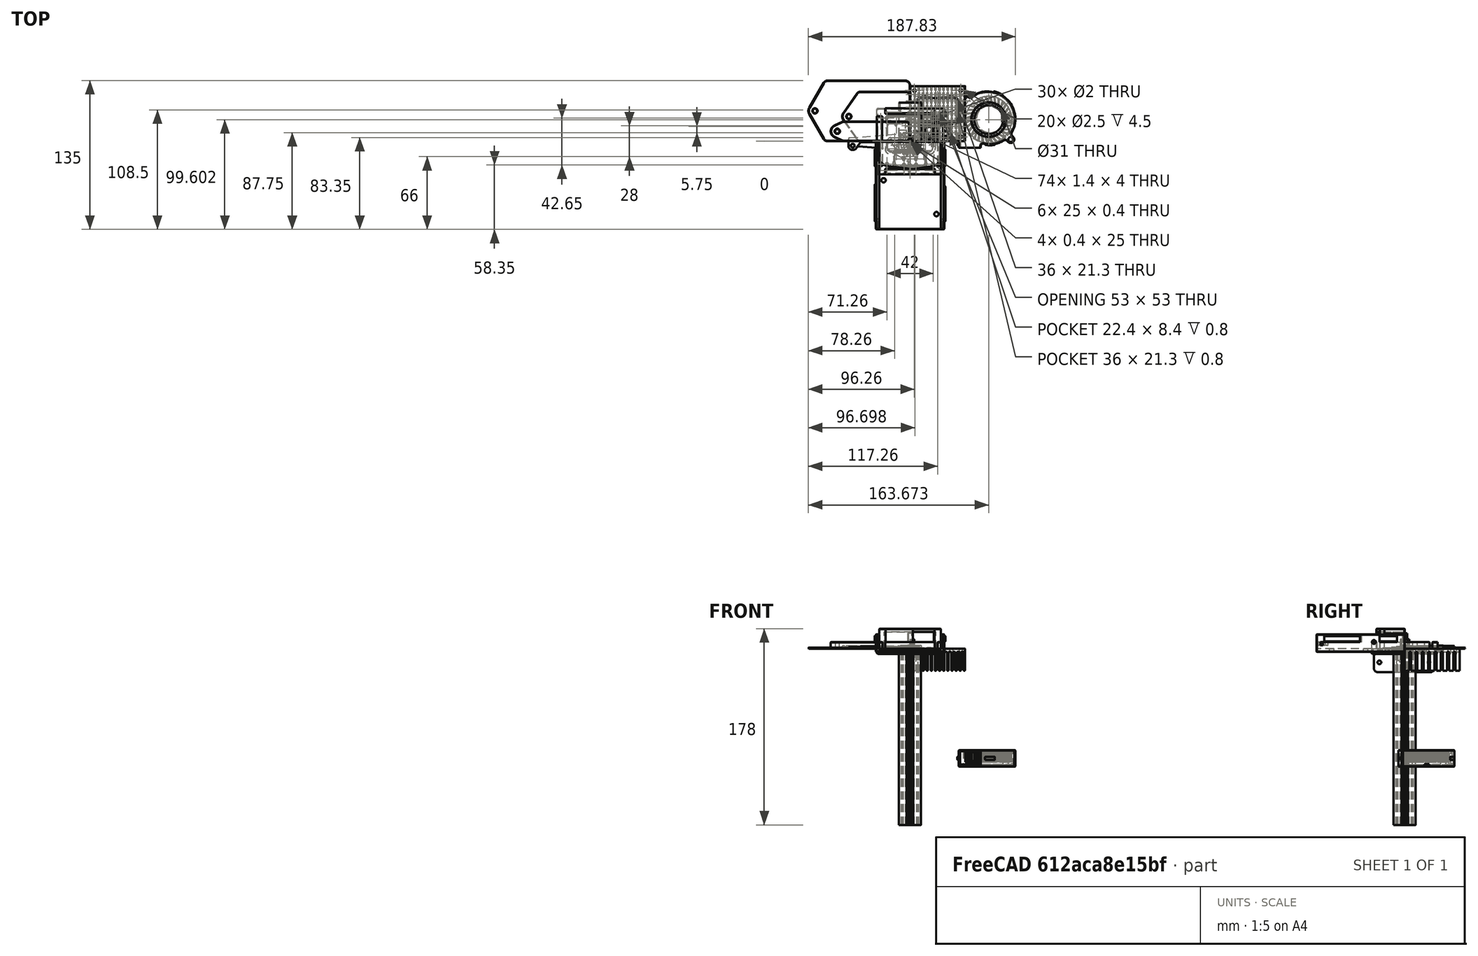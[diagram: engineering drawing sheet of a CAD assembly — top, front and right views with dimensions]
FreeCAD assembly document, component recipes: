
FREECAD ASSEMBLY — COMPONENT RECIPES ("bedburner")

This assembly document has 27 components, labeled P0..P26 below (a component is one placed body or linked part). 7 of them carry a construction recipe — the FreeCAD feature program that regenerates the part from scratch, quoted from this document or its linked companion documents; the rest are supplied as boundary geometry only. No exploded tour is included for this assembly.
COMPONENT P0 — geometry summary ("HFS5-2020-161"; no construction recipe available for this part):
  bounding box: 160.0 x 20.0 x 20.0 mm
  tessellated surface: 1,048 triangles
  volume: 29141 mm^3 (46% of its bounding box)
  symmetry: 2-fold rotationally symmetric about the x axis; 4-fold rotationally symmetric about the y axis; 2-fold rotationally symmetric about the z axis; mirror-symmetric across its x mid-plane, y mid-plane, z mid-plane
COMPONENT P1 — geometry summary ("fan_radial_50x016"; no construction recipe available for this part):
  bounding box: 55.3 x 54.7 x 15.0 mm
  tessellated surface: 21,378 triangles
  volume: 17025 mm^3 (37% of its bounding box)
COMPONENT P2 — recipe-attached ("heater_bracket001", modeled in this document).
Construction recipe (the document's own serialized feature program — sketch geometry with constraints, then the solid features built on it; lengths are millimeters unless a unit is written):

FEATURE [Sketcher::SketchObject] Sketch085  label="hrb_block_plate_s"
  ArcFitTolerance = 0
  AttachmentSupport = -> [XY_Plane138]
  ExternalTypes = [0]
  FullyConstrained = true
  MakeInternals = false
  MapMode = 5
  _ExternalGeoVersion = 0
  expr: .Constraints.bend_straight = <<bracket_params>>.feature_bend_straight
  expr: .Constraints.block_screw_spacing = <<block_params>>.heatsink_screw_spacing
  expr: .Constraints.block_side_offset = <<bracket_params>>.feature_block_offset
  expr: .Constraints.block_width = <<block_params>>.heatsink_width
  expr: .Constraints.height_block_bottom = <<bracket_params>>.feature_deck_clear_block
  expr: .Constraints.height_block_top = <<bracket_params>>.feature_deck_clear_block + <<block_params>>.heatsink_height
  expr: .Constraints.height_bracket_bottom = <<bracket_params>>.feature_deck_clear_bracket
  expr: .Constraints.height_component_top = <<bracket_params>>.feature_deck_clear_block + <<block_params>>.heatsink_height + <<bracket_params>>.height_componets
  expr: .Constraints.height_extrusion = <<bracket_params>>.height_extrusion
  expr: .Constraints.height_stock_bed = <<bracket_params>>.height_extrusion + <<bracket_params>>.height_stock
  expr: .Constraints.height_stock_silicone = <<bracket_params>>.height_extrusion + <<bracket_params>>.height_stock - <<bracket_params>>.height_silicone_heater
  expr: .Constraints.height_whop_bed = <<bracket_params>>.height_extrusion + <<bracket_params>>.height_whopKinematic
  expr: .Constraints.height_whop_silicone = <<bracket_params>>.height_extrusion + <<bracket_params>>.height_whopKinematic - <<bracket_params>>.height_silicone_heater
  expr: .Constraints.plate_block_overlap = <<bracket_params>>.rear_overlap
  expr: .Constraints.plate_overhang = <<bracket_params>>.rear_overhang_inner
  expr: .Constraints.plate_overhang_outer = <<bracket_params>>.rear_overhang_outer
  expr: .Constraints.screw_head = <<bracket_params>>.feature_screw_head
  expr: .Constraints.screw_hole = <<bracket_params>>.feature_screw_hole
  expr: .Constraints.screw_pad_diam = <<bracket_params>>.rear_pad_diam
  expr: .Constraints.side_extension = <<bracket_params>>.rear_side_extension
  expr: .Constraints.side_screw_inset1 = <<bracket_params>>.rear_side_screw_inset
  expr: .Constraints.side_screw_inset2 = <<bracket_params>>.rear_side_screw_inset + <<bracket_params>>.rear_side_screw_spacing
  sketch-geometry (50):
    g0: Circle CenterX=-10 CenterY=-4 CenterZ=0 NormalX=0 NormalY=0 NormalZ=1 AngleXU=0 Radius=1.7
    g1: Circle CenterX=-52 CenterY=-4 CenterZ=0 NormalX=0 NormalY=0 NormalZ=1 AngleXU=0 Radius=1.7
    g2: ArcOfCircle CenterX=-52 CenterY=-4 CenterZ=0 NormalX=0 NormalY=0 NormalZ=1 AngleXU=0 Radius=4 StartAngle=3.14159 EndAngle=5.67232
    g3: ArcOfCircle CenterX=-10 CenterY=-4 CenterZ=0 NormalX=0 NormalY=0 NormalZ=1 AngleXU=0 Radius=4 StartAngle=3.75246 EndAngle=6.28319
    g4: LineSegment [constr] StartX=-52 StartY=-2.3 StartZ=0 EndX=-52 EndY=0 EndZ=0
    g5: LineSegment StartX=-48.7234 StartY=-6.29431 StartZ=0 EndX=-45.0163 EndY=-1 EndZ=0
    g6: LineSegment StartX=-13.2766 StartY=-6.29431 StartZ=0 EndX=-16.9837 EndY=-1 EndZ=0
    g7: LineSegment StartX=-56 StartY=-4 StartZ=0 EndX=-56 EndY=3 EndZ=0
    g8: LineSegment StartX=-45.0163 StartY=-1 StartZ=0 EndX=-16.9837 EndY=-1 EndZ=0
    g9: LineSegment StartX=-6 StartY=-1 StartZ=0 EndX=-6 EndY=-4 EndZ=0
    g10: LineSegment StartX=-6 StartY=-1 StartZ=0 EndX=0 EndY=-1 EndZ=0
    g11: LineSegment StartX=0 StartY=-1 StartZ=0 EndX=0 EndY=7 EndZ=0
    g12: LineSegment [constr] StartX=0 StartY=0 StartZ=0 EndX=20 EndY=0 EndZ=0
    g13: LineSegment [constr] StartX=20 StartY=0 StartZ=0 EndX=20 EndY=-20 EndZ=0
    g14: LineSegment [constr] StartX=20 StartY=-20 StartZ=0 EndX=0 EndY=-20 EndZ=0
    g15: LineSegment [constr] StartX=0 StartY=-20 StartZ=0 EndX=0 EndY=0 EndZ=0
    g16: Circle [constr] CenterX=10 CenterY=-10 CenterZ=0 NormalX=0 NormalY=0 NormalZ=1 AngleXU=0 Radius=10
    g17: LineSegment [constr] StartX=29.5 StartY=0 StartZ=0 EndX=29.5 EndY=-20 EndZ=0
    g18: LineSegment [constr] StartX=35.5 StartY=0 StartZ=0 EndX=35.5 EndY=-20 EndZ=0
    g19: LineSegment [constr] StartX=29.5 StartY=-20 StartZ=0 EndX=27.5 EndY=-20 EndZ=0
    g20: LineSegment [constr] StartX=27.5 StartY=-20 StartZ=0 EndX=27.5 EndY=-10 EndZ=0
    g21: LineSegment [constr] StartX=35.5 StartY=-20 StartZ=0 EndX=33.5 EndY=-20 EndZ=0
    g22: LineSegment [constr] StartX=33.5 StartY=-20 StartZ=0 EndX=33.5 EndY=-10 EndZ=0
    g23: Circle [constr] CenterX=0 CenterY=5 CenterZ=0 NormalX=0 NormalY=0 NormalZ=1 AngleXU=0 Radius=1.7
    g24: Circle [constr] CenterX=0 CenterY=5 CenterZ=0 NormalX=0 NormalY=0 NormalZ=1 AngleXU=0 Radius=2.75
    g25: Circle [constr] CenterX=0 CenterY=22 CenterZ=0 NormalX=0 NormalY=0 NormalZ=1 AngleXU=0 Radius=1.7
    g26: Circle [constr] CenterX=0 CenterY=22 CenterZ=0 NormalX=0 NormalY=0 NormalZ=1 AngleXU=0 Radius=2.75
    g27: LineSegment [constr] StartX=0 StartY=27 StartZ=0 EndX=0 EndY=23.7 EndZ=0
    g28: LineSegment StartX=-56 StartY=3 StartZ=0 EndX=-4 EndY=7 EndZ=0
    g29: LineSegment StartX=-4 StartY=7 StartZ=0 EndX=0 EndY=7 EndZ=0
    g30: LineSegment [constr] StartX=-56 StartY=0 StartZ=0 EndX=-56 EndY=-50 EndZ=0
    g31: LineSegment [constr] StartX=-56 StartY=-50 StartZ=0 EndX=-6 EndY=-50 EndZ=0
    g32: LineSegment [constr] StartX=-6 StartY=-50 StartZ=0 EndX=-6 EndY=0 EndZ=0
    g33: LineSegment [constr] StartX=-6 StartY=0 StartZ=0 EndX=-56 EndY=0 EndZ=0
    g34: LineSegment [constr] StartX=-52 StartY=-4 StartZ=0 EndX=-52 EndY=-46 EndZ=0
    g35: LineSegment [constr] StartX=-52 StartY=-46 StartZ=0 EndX=-10 EndY=-46 EndZ=0
    g36: LineSegment [constr] StartX=-10 StartY=-46 StartZ=0 EndX=-10 EndY=-4 EndZ=0
    g37: LineSegment [constr] StartX=-10 StartY=-4 StartZ=0 EndX=-52 EndY=-4 EndZ=0
    g38: Circle [constr] CenterX=-31 CenterY=-25 CenterZ=0 NormalX=0 NormalY=0 NormalZ=1 AngleXU=0 Radius=21
    g39: Circle [constr] CenterX=-31 CenterY=-25 CenterZ=0 NormalX=0 NormalY=0 NormalZ=1 AngleXU=0 Radius=25
    g40: Circle [constr] CenterX=-10 CenterY=-4 CenterZ=0 NormalX=0 NormalY=0 NormalZ=1 AngleXU=0 Radius=2.75
    g41: Circle [constr] CenterX=-52 CenterY=-4 CenterZ=0 NormalX=0 NormalY=0 NormalZ=1 AngleXU=0 Radius=2.75
    g42: LineSegment [constr] StartX=29 StartY=0 StartZ=0 EndX=22.5 EndY=0 EndZ=0
    g43: LineSegment [constr] StartX=22.5 StartY=-10 StartZ=0 EndX=29 EndY=-10 EndZ=0
    g44: LineSegment [constr] StartX=29 StartY=-10 StartZ=0 EndX=29 EndY=0 EndZ=0
    g45: LineSegment [constr] StartX=2.5 StartY=0 StartZ=0 EndX=2.5 EndY=-20 EndZ=0
    g46: LineSegment [constr] StartX=2.5 StartY=-20 StartZ=0 EndX=22.5 EndY=-20 EndZ=0
    g47: LineSegment [constr] StartX=22.5 StartY=-20 StartZ=0 EndX=22.5 EndY=0 EndZ=0
    g48: LineSegment [constr] StartX=22.5 StartY=0 StartZ=0 EndX=2.5 EndY=0 EndZ=0
    g49: LineSegment [constr] StartX=1 StartY=0 StartZ=0 EndX=1 EndY=-20 EndZ=0
  constraints (147):
    c: Equal(g0,g1)
    c: Diameter(g1) = 3.4  'screw_hole'
    c: Coincident(g2,g1)
    c: Coincident(g3,g0)
    c: Equal(g2,g3)
    c: PointOnObject(g4,g1)
    c: PointOnObject(g4,g2)
    c: Vertical(g4)
    c: PointOnObject(g1,g4)
    c: Diameter(g2) = 8  'screw_pad_diam'
    c: Vertical(g7)
    c: Tangent(g7,g2) = 1.5708
    c: Tangent(g2,g5) = -1.5708
    c: Tangent(g6,g3) = 1.5708
    c: Coincident(g8,g5)
    c: Coincident(g8,g6)
    c: Horizontal(g8)
    c: Equal(g5,g6)
    c: Angle(g5,g7) = 0.610865  'screw_pad_angle'
    c: Distance(g8) = 28.0326  'plate_overlay_width'
    c: Vertical(g9)
    c: Coincident(g10,g9)
    c: PointOnObject(g10,g-2)
    c: Horizontal(g10)
    c: Tangent(g9,g3) = 1.5708
    c: Coincident(g11,g10)
    c: PointOnObject(g11,g-2)
    c: DistanceY(g-1,g11) = 7  'plate_overhang'
    c: PointOnObject(g10,g8)
    c: Coincident(g12,g13)
    c: Coincident(g13,g14)
    c: Coincident(g14,g15)
    c: Coincident(g15,g12)
    c: Horizontal(g12)
    c: Horizontal(g14)
    c: Vertical(g13)
    c: Vertical(g15)
    c: Tangent(g15,g16)
    c: Tangent(g16,g12)
    c: Tangent(g16,g13)
    c: Tangent(g14,g16)
    c: Distance(g14) = 20  'height_extrusion'
    c: Vertical(g17)
    c: Vertical(g18)
    c: PointOnObject(g17,g14)
    c: PointOnObject(g18,g14)
    c: PointOnObject(g17,g12)
    c: PointOnObject(g18,g12)
    c: Coincident(g19,g17)
    c: Coincident(g20,g19)
    c: Coincident(g21,g18)
    c: Coincident(g22,g21)
    c: Vertical(g22)
    c: Horizontal(g21)
    c: Horizontal(g19)
    c: Coincident(g24,g23)
    c: Coincident(g26,g25)
    c: Equal(g23,g25)
    c: Equal(g26,g24)
    c: Equal(g23,g0)
    c: PointOnObject(g25,g-2)
    c: PointOnObject(g23,g-2)
    c: PointOnObject(g27,g25)
    c: PointOnObject(g27,g-2)
    c: PointOnObject(g27,g-2)
    c: Distance(g27) = 3.3  'side_screw_outer'
    c: DistanceY(g11,g27) = 20  'side_extension'
    c: Coincident(g7,g28)
    c: Coincident(g28,g29)
    c: Coincident(g29,g11)
    c: Horizontal(g29)
    c: DistanceX(g29,g29) = 4  'bend_straight'
    c: Coincident(g30,g31)
    c: Coincident(g31,g32)
    c: Coincident(g32,g33)
    c: Coincident(g33,g30)
    c: Vertical(g30)
    c: Vertical(g32)
    c: Horizontal(g31)
    c: Horizontal(g33)
    c: Coincident(g34,g35)
    c: Coincident(g35,g36)
    c: Coincident(g36,g37)
    c: Coincident(g37,g34)
    c: Vertical(g34)
    c: Vertical(g36)
    c: Horizontal(g35)
    c: Horizontal(g37)
    c: Coincident(g39,g38)
    c: Tangent(g39,g33)
    c: Tangent(g39,g32)
    c: Tangent(g39,g31)
    c: Tangent(g39,g30)
    c: Diameter(g39) = 50  'block_width'
    c: Tangent(g37,g38)
    c: Tangent(g38,g36)
    c: Tangent(g38,g35)
    c: Tangent(g38,g34)
    c: Diameter(g38) = 42  'block_screw_spacing'
    c: Distance(g6,g-1) = 1  'plate_block_overlap'
    c: DistanceY(g-1,g7) = 3  'plate_overhang_outer'
    c: Coincident(g34,g1)
    c: Coincident(g36,g0)
    c: PointOnObject(g32,g-1)
    c: Distance(g32,g-1) = 6  'block_side_offset'
    c: Coincident(g40,g0)
    c: Coincident(g41,g1)
    c: Equal(g24,g40)
    c: Equal(g40,g41)
    c: Diameter(g41) = 5.5  'screw_head'
    c: DistanceY(g-1,g23) = 5  'side_screw_inset1'
    c: DistanceY(g-1,g25) = 22  'side_screw_inset2'
    c: Coincident(g12,g-1)
    c: DistanceX(g-1,g17) = 29.5  'height_stock_bed'
    c: DistanceX(g-1,g19) = 27.5  'height_stock_silicone'
    c: DistanceX(g-1,g21) = 33.5  'height_whop_silicone'
    c: DistanceX(g-1,g18) = 35.5  'height_whop_bed'
    c: Coincident(g43,g44)
    c: Coincident(g44,g42)
    c: Horizontal(g42)
    c: Horizontal(g43)
    c: Vertical(g44)
    c: PointOnObject(g20,g43)
    c: PointOnObject(g22,g43)
    c: PointOnObject(g16,g43)
    c: PointOnObject(g42,g-1)
    c: Coincident(g45,g46)
    c: Coincident(g46,g47)
    c: Coincident(g47,g48)
    c: Coincident(g48,g45)
    c: Vertical(g45)
    c: Vertical(g47)
    c: Horizontal(g46)
    c: Horizontal(g48)
    c: Coincident(g47,g42)
    c: PointOnObject(g43,g47)
    c: Vertical(g49)
    c: PointOnObject(g49,g12)
    c: PointOnObject(g49,g14)
    c: DistanceX(g-1,g45) = 2.5  'height_block_bottom'
    c: PointOnObject(g45,g14)
    c: DistanceX(g-1,g49) = 1  'height_bracket_bottom'
    c: DistanceX(g-1,g46) = 22.5  'height_block_top'
    c: DistanceX(g-1,g43) = 29  'height_component_top'
    c: DistanceX(g43,g22) = 4.5  'height_clear_whop'
    c: DistanceX(g19,g43) = 1.5  'height_crash_stock'
    c: Vertical(g20)
FEATURE [Sketcher::SketchObject] Sketch086  label="hrb_side_features_s"
  ArcFitTolerance = 0
  AttachmentSupport = -> [YZ_Plane138]
  ExternalTypes = [0]
  FullyConstrained = true
  MakeInternals = false
  MapMode = 5
  Placement = pos=(0,0,0) rot=(0.57735,0.57735,0.57735;2.0944rad)
  _ExternalGeoVersion = 0
  expr: .Constraints.cut_end = <<bracket_params>>.rear_overhang_inner + <<bracket_params>>.rear_side_extension + 1 mm
  expr: .Constraints.plate_overhang = <<bracket_params>>.rear_overhang_inner
  expr: .Constraints.screw_head = <<bracket_params>>.feature_screw_head
  expr: .Constraints.screw_height = <<bracket_params>>.feature_side_height + <<bracket_params>>.feature_deck_clear_bracket - <<bracket_params>>.height_extrusion / 2
  expr: .Constraints.screw_hole = <<bracket_params>>.feature_screw_hole
  expr: .Constraints.screw_inset1 = <<bracket_params>>.rear_side_screw_inset
  expr: .Constraints.screw_inset2 = <<bracket_params>>.rear_side_screw_inset + <<bracket_params>>.rear_side_screw_spacing
  expr: .Constraints.side_recess_top = <<bracket_params>>.feature_side_height + <<bracket_params>>.feature_deck_clear_bracket - <<bracket_params>>.height_extrusion + <<bracket_params>>.feature_side_recess
  sketch-geometry (9):
    g0: Circle CenterX=5 CenterY=-12.5 CenterZ=0 NormalX=0 NormalY=0 NormalZ=1 AngleXU=0 Radius=1.7
    g1: Circle CenterX=22 CenterY=-12.5 CenterZ=0 NormalX=0 NormalY=0 NormalZ=1 AngleXU=0 Radius=1.7
    g2: LineSegment [constr] StartX=5 StartY=-12.5 StartZ=0 EndX=22 EndY=-12.5 EndZ=0
    g3: Circle [constr] CenterX=5 CenterY=-12.5 CenterZ=0 NormalX=0 NormalY=0 NormalZ=1 AngleXU=0 Radius=2.75
    g4: Circle [constr] CenterX=22 CenterY=-12.5 CenterZ=0 NormalX=0 NormalY=0 NormalZ=1 AngleXU=0 Radius=2.75
    g5: LineSegment StartX=28 StartY=-3.5 StartZ=0 EndX=28 EndY=0 EndZ=0
    g6: LineSegment StartX=7 StartY=0 StartZ=0 EndX=7 EndY=-3.5 EndZ=0
    g7: LineSegment StartX=7 StartY=-3.5 StartZ=0 EndX=28 EndY=-3.5 EndZ=0
    g8: LineSegment StartX=7 StartY=0 StartZ=0 EndX=28 EndY=0 EndZ=0
  constraints (24):
    c: Coincident(g2,g0)
    c: Coincident(g2,g1)
    c: Horizontal(g2)
    c: Diameter(g0) = 3.4  'screw_hole'
    c: Equal(g1,g0)
    c: Coincident(g3,g0)
    c: Coincident(g4,g1)
    c: Diameter(g3) = 5.5  'screw_head'
    c: Equal(g3,g4)
    c: Coincident(g6,g7)
    c: Coincident(g7,g5)
    c: Vertical(g5)
    c: Vertical(g6)
    c: Horizontal(g7)
    c: PointOnObject(g5,g-1)
    c: Coincident(g8,g6)
    c: PointOnObject(g6,g-1)
    c: DistanceX(g-1,g6) = 7  'plate_overhang'
    c: Coincident(g8,g5)
    c: DistanceX(g-1,g5) = 28  'cut_end'
    c: DistanceY(g0,g-1) = 12.5  'screw_height'
    c: DistanceX(g-1,g0) = 5  'screw_inset1'
    c: DistanceX(g-1,g1) = 22  'screw_inset2'
    c: DistanceY(g6,g-1) = 3.5  'side_recess_top'
FEATURE [PartDesign::FeaturePython] BaseBend  label="hrb_block_plate"  # WARN: FeaturePython — macro-defined, semantics opaque (R4)
  BendSide = 0
  BendSketch = -> Sketch085
  MidPlane = false
  Reverse = false
  Suppressed = false
  length = 100
  radius = 1.6
  thickness = 1.5
  expr: radius = <<bracket_params>>.material_bend
  expr: thickness = <<bracket_params>>.material_thickness
FEATURE [PartDesign::FeaturePython] Bend  label="hrb_side_bend"  # WARN: FeaturePython — macro-defined, semantics opaque (R4)
  AutoMiter = true
  BaseFeature = -> BaseBend
  BendType = 1
  LengthList = [21.5]
  LengthSpec = 2
  NonperforationMaxLength = 5
  Perforate = false
  PerforationAngle = 0
  PerforationInitialLength = 5
  PerforationMaxLength = 5
  ReliefFactor = 0.7
  Suppressed = false
  UseReliefFactor = false
  angle = 90
  baseObject = -> BaseBend [Edge27]
  bendAList = [90]
  extend1 = 0
  extend2 = 0
  gap1 = 0
  gap2 = 0
  invert = false
  kfactor = 0.5
  length = 21.5
  maxExtendDist = 5
  minGap = 0.2
  minReliefGap = 1
  miterangle1 = 0
  miterangle2 = 0
  offset = 0
  radius = 1.6
  reliefType = 0
  reliefd = 1
  reliefw = 0.8
  sketchflip = false
  sketchinvert = false
  unfold = false
  expr: length = <<bracket_params>>.feature_side_height
  expr: radius = <<bracket_params>>.material_bend
FEATURE [PartDesign::FeaturePython] Extend  label="hrb_side_ext"  # WARN: FeaturePython — macro-defined, semantics opaque (R4)
  BaseFeature = -> Bend
  Offset = 0.02
  Refine = true
  Suppressed = false
  UseSubtraction = false
  baseObject = -> Bend [Face21]
  gap1 = 0
  gap2 = 0
  length = 20
  expr: length = <<bracket_params>>.rear_side_extension
FEATURE [PartDesign::Pocket] Pocket  label="hrb_side_features"
  BaseFeature = -> Extend
  Direction = (-1,0,0)
  Length = 1.5
  Length2 = 5
  Profile = -> Sketch086
  ReferenceAxis = -> Sketch086 [N_Axis]
  Refine = true
  SideType = 0
  Suppressed = false
  Type = 0
  Type2 = 0
  expr: Length = <<bracket_params>>.material_thickness
FEATURE [PartDesign::Fillet] Fillet  label="hrb_outer_flt"
  Base = -> Pocket [Edge2]
  BaseFeature = -> Pocket
  Radius = 1.5
  Refine = true
  SupportTransform = false
  Suppressed = false
  UseAllEdges = false
FEATURE [PartDesign::Fillet] Fillet014  label="hrb_side_flt"
  Base = -> Fillet [Edge59,Edge46,Edge65]
  BaseFeature = -> Fillet
  Radius = 4
  Refine = true
  SupportTransform = false
  Suppressed = false
  UseAllEdges = false
FEATURE [PartDesign::Fillet] Fillet015  label="hrb_ext_flt"
  Base = -> Fillet014 [Edge62]
  BaseFeature = -> Fillet014
  Radius = 1.5
  Refine = true
  SupportTransform = false
  Suppressed = false
  UseAllEdges = false
FEATURE [PartDesign::Fillet] Fillet019  label="hrb_overlay_flt"
  Base = -> Fillet015 [Edge75,Edge76]
  BaseFeature = -> Fillet015
  Radius = 1.5
  Refine = true
  SupportTransform = false
  Suppressed = false
  UseAllEdges = false
FEATURE [PartDesign::Body] Body048  label="heater_rear_bracket"
  AllowCompound = false
  Group = -> [Sketch085,Sketch086,BaseBend,Bend,Extend,Pocket,Fillet,Fillet014,Fillet015,Fillet019]
  Origin = -> Origin138
  Tip = -> Fillet019
COMPONENT P3 — recipe-attached ("heater_fan_duct001", modeled in this document).
Construction recipe (the document's own serialized feature program — sketch geometry with constraints, then the solid features built on it; lengths are millimeters unless a unit is written):

FEATURE [Sketcher::SketchObject] Sketch  label="hfd_base_s"
  ArcFitTolerance = 1e-06
  AttachmentSupport = -> [XY_Plane140]
  ExternalTypes = [0]
  FullyConstrained = true
  MakeInternals = false
  MapMode = 5
  _ExternalGeoVersion = 0
  expr: .Constraints.base_width = <<block_params>>.heatsink_width + 2 * <<bracket_params>>.feature_block_offset
  expr: .Constraints.ref_block_spacing = <<bracket_params>>.feature_block_offset
  expr: .Constraints.ref_block_width = <<block_params>>.heatsink_width
  sketch-geometry (65):
    g0: LineSegment [constr] StartX=21.7128 StartY=-20.5407 StartZ=0 EndX=-28.635 EndY=-28.6713 EndZ=0
    g1: LineSegment [constr] StartX=-28.635 StartY=-28.6713 StartZ=0 EndX=-20.5044 EndY=-79.019 EndZ=0
    g2: LineSegment [constr] StartX=-20.5044 StartY=-79.019 StartZ=0 EndX=29.8433 EndY=-70.8884 EndZ=0
    g3: LineSegment [constr] StartX=29.8433 StartY=-70.8884 StartZ=0 EndX=21.7128 EndY=-20.5407 EndZ=0
    g4: LineSegment [constr] StartX=2.46216 StartY=-23.6495 StartZ=0 EndX=2.781 EndY=-25.6239 EndZ=0
    g5: Circle [constr] CenterX=24 CenterY=-66.1595 CenterZ=0 NormalX=0 NormalY=0 NormalZ=1 AngleXU=0 Radius=2.25
    g6: Circle [constr] CenterX=-24 CenterY=-35.4187 CenterZ=0 NormalX=0 NormalY=0 NormalZ=1 AngleXU=0 Radius=2.25
    g7: Circle [constr] CenterX=-1.38618 CenterY=-50 CenterZ=0 NormalX=0 NormalY=0 NormalZ=1 AngleXU=0 Radius=16.25
    g8: LineSegment [constr] StartX=-5.43552 StartY=-24.9249 StartZ=0 EndX=-1.38618 EndY=-50 EndZ=0
    g9: LineSegment [constr] StartX=-1.38618 StartY=-50 StartZ=0 EndX=2.69506 EndY=-75.2726 EndZ=0
    g10: LineSegment [constr] StartX=-24.5856 StartY=-53.7464 StartZ=0 EndX=-1.38618 EndY=-50 EndZ=0
    g11: LineSegment [constr] StartX=-1.38618 StartY=-50 StartZ=0 EndX=25.7621 EndY=-45.6159 EndZ=0
    g12: LineSegment [constr] StartX=-25 StartY=50 StartZ=0 EndX=-25 EndY=0 EndZ=0
    g13: LineSegment [constr] StartX=-25 StartY=0 StartZ=0 EndX=25 EndY=0 EndZ=0
    g14: LineSegment [constr] StartX=25 StartY=0 StartZ=0 EndX=25 EndY=50 EndZ=0
    g15: LineSegment [constr] StartX=25 StartY=50 StartZ=0 EndX=-25 EndY=50 EndZ=0
    g16: LineSegment [constr] StartX=-24 StartY=-35.4187 StartZ=0 EndX=24 EndY=-66.1595 EndZ=0
    g17: LineSegment [constr] StartX=-21.1304 StartY=-53.1885 StartZ=0 EndX=-24 EndY=-35.4187 EndZ=0
    g18: LineSegment [constr] StartX=-24 StartY=-35.4187 StartZ=0 EndX=-4.25579 EndY=-32.2302 EndZ=0
    g19: LineSegment [constr] StartX=20.8115 StartY=-46.4153 StartZ=0 EndX=24 EndY=-66.1595 EndZ=0
    g20: LineSegment [constr] StartX=24 StartY=-66.1595 StartZ=0 EndX=1.80229 EndY=-69.7442 EndZ=0
    g21: LineSegment [constr] StartX=25 StartY=0 StartZ=0 EndX=31 EndY=0 EndZ=0
    g22: LineSegment [constr] StartX=-25 StartY=0 StartZ=0 EndX=-31 EndY=0 EndZ=0
    g23: LineSegment [constr] StartX=8.51935 StartY=0 StartZ=0 EndX=12.0875 EndY=-22.0951 EndZ=0
    g24: LineSegment [constr] StartX=-31 StartY=0 StartZ=0 EndX=-31 EndY=-50 EndZ=0
    g25: LineSegment [constr] StartX=-31 StartY=-50 StartZ=0 EndX=-31 EndY=-100 EndZ=0
    g26: LineSegment [constr] StartX=-31 StartY=-100 StartZ=0 EndX=-31 EndY=-150 EndZ=0
    g27: LineSegment [constr] StartX=31 StartY=0 StartZ=0 EndX=31 EndY=-50 EndZ=0
    g28: LineSegment [constr] StartX=31 StartY=-50 StartZ=0 EndX=31 EndY=-100 EndZ=0
    g29: LineSegment [constr] StartX=31 StartY=-100 StartZ=0 EndX=31 EndY=-150 EndZ=0
    g30: Circle [constr] CenterX=-24 CenterY=-35.4187 CenterZ=0 NormalX=0 NormalY=0 NormalZ=1 AngleXU=0 Radius=3.5
    g31: Circle [constr] CenterX=24 CenterY=-66.1595 CenterZ=0 NormalX=0 NormalY=0 NormalZ=1 AngleXU=0 Radius=3.5
    g32: LineSegment [constr] StartX=31 StartY=-66.1595 StartZ=0 EndX=27.5 EndY=-66.1595 EndZ=0
    g33: ArcOfCircle [constr] CenterX=9.43542 CenterY=-50.8861 CenterZ=0 NormalX=0 NormalY=0 NormalZ=1 AngleXU=0 Radius=16.9581 StartAngle=5.41384 EndAngle=6.44329
    g34: ArcOfCircle [constr] CenterX=-2.46465 CenterY=-50.1742 CenterZ=0 NormalX=0 NormalY=0 NormalZ=1 AngleXU=0 Radius=22.4076 StartAngle=2.53575 EndAngle=3.3017
    g35: LineSegment [constr] StartX=21.7128 StartY=-20.5407 StartZ=0 EndX=18.3957 EndY=0 EndZ=0
    g36: LineSegment [constr] StartX=2.46216 StartY=-23.6495 StartZ=0 EndX=-1.35696 EndY=0 EndZ=0
    g37: Circle CenterX=-24 CenterY=-35.4187 CenterZ=0 NormalX=0 NormalY=0 NormalZ=1 AngleXU=0 Radius=2
    g38: Circle CenterX=24 CenterY=-66.1595 CenterZ=0 NormalX=0 NormalY=0 NormalZ=1 AngleXU=0 Radius=2
    g39: LineSegment StartX=-31 StartY=0 StartZ=0 EndX=-31 EndY=-80 EndZ=0
    g40: LineSegment StartX=-31 StartY=-80 StartZ=0 EndX=31 EndY=-80 EndZ=0
    g41: LineSegment StartX=31 StartY=-80 StartZ=0 EndX=31 EndY=0 EndZ=0
    g42: LineSegment StartX=31 StartY=0 StartZ=0 EndX=-31 EndY=0 EndZ=0
    g43: LineSegment [constr] StartX=-31 StartY=-19.6 StartZ=0 EndX=-31 EndY=-36.4 EndZ=0
    g44: LineSegment [constr] StartX=-31 StartY=-36.4 StartZ=0 EndX=-28 EndY=-36.4 EndZ=0
    g45: LineSegment [constr] StartX=-28 StartY=-19.6 StartZ=0 EndX=-31 EndY=-19.6 EndZ=0
    g46: LineSegment [constr] StartX=-28 StartY=-19.6 StartZ=0 EndX=-28 EndY=-25.2 EndZ=0
    g47: LineSegment [constr] StartX=-28 StartY=-25.2 StartZ=0 EndX=-28 EndY=-30.8 EndZ=0
    g48: LineSegment [constr] StartX=-28 StartY=-30.8 StartZ=0 EndX=-28 EndY=-36.4 EndZ=0
    g49: LineSegment [constr] StartX=28 StartY=-19.6 StartZ=0 EndX=28 EndY=-25.2 EndZ=0
    g50: LineSegment [constr] StartX=28 StartY=-25.2 StartZ=0 EndX=28 EndY=-30.8 EndZ=0
    g51: LineSegment [constr] StartX=28 StartY=-30.8 StartZ=0 EndX=28 EndY=-36.4 EndZ=0
    g52: LineSegment [constr] StartX=28 StartY=-36.4 StartZ=0 EndX=31 EndY=-36.4 EndZ=0
    g53: LineSegment [constr] StartX=31 StartY=-36.4 StartZ=0 EndX=31 EndY=-19.6 EndZ=0
    g54: LineSegment [constr] StartX=31 StartY=-19.6 StartZ=0 EndX=28 EndY=-19.6 EndZ=0
    g55: LineSegment [constr] StartX=-28 StartY=-25.2 StartZ=0 EndX=-28 EndY=-30.8 EndZ=0
    g56: LineSegment [constr] StartX=-28 StartY=-30.8 StartZ=0 EndX=-25.2 EndY=-30.8 EndZ=0
    g57: LineSegment [constr] StartX=-25.2 StartY=-30.8 StartZ=0 EndX=-25.2 EndY=-25.2 EndZ=0
    g58: LineSegment [constr] StartX=-25.2 StartY=-25.2 StartZ=0 EndX=-28 EndY=-25.2 EndZ=0
    g59: LineSegment [constr] StartX=28 StartY=-25.2 StartZ=0 EndX=25.2 EndY=-25.2 EndZ=0
    g60: LineSegment [constr] StartX=25.2 StartY=-25.2 StartZ=0 EndX=25.2 EndY=-30.8 EndZ=0
    g61: LineSegment [constr] StartX=25.2 StartY=-30.8 StartZ=0 EndX=28 EndY=-30.8 EndZ=0
    g62: LineSegment [constr] StartX=28 StartY=-30.8 StartZ=0 EndX=28 EndY=-25.2 EndZ=0
    g63: LineSegment [constr] StartX=31 StartY=-28 StartZ=0 EndX=28 EndY=-28 EndZ=0
    g64: LineSegment [constr] StartX=-31 StartY=-28 StartZ=0 EndX=-28 EndY=-28 EndZ=0
  constraints (186):
    c: Coincident(g0,g1)
    c: Coincident(g1,g2)
    c: Coincident(g2,g3)
    c: Coincident(g3,g0)
    c: Parallel(g0,g2)
    c: Perpendicular(g2,g3)
    c: Perpendicular(g1,g2)
    c: Perpendicular(g0,g4)
    c: Diameter(g7) = 32.5  'fan_spec_open'
    c: Equal(g6,g5)
    c: Diameter(g5) = 4.5  'fan_spec_screw_diam'
    c: Coincident(g8,g9)
    c: Coincident(g8,g7)
    c: Perpendicular(g8,g0) = 4.71239
    c: Perpendicular(g9,g2) = 1.5708
    c: Coincident(g10,g7)
    c: Coincident(g10,g11)
    c: Perpendicular(g11,g3) = 1.5708
    c: Perpendicular(g10,g1) = 4.71239
    c: Distance(g8,g8) = 25.4  'fan_spec_center_offset1'
    c: Distance(g11,g11) = 27.5  'fan_spec_center_offset2'
    c: Coincident(g12,g13)
    c: Coincident(g13,g14)
    c: Coincident(g14,g15)
    c: Coincident(g15,g12)
    c: Vertical(g12)
    c: Vertical(g14)
    c: Horizontal(g13)
    c: Equal(g15,g12)
    c: Symmetric(g12,g14,g-2)
    c: Distance(g1,g1) = 51  'fan_spec_width1'
    c: Distance(g2,g2) = 51  'fan_spec_width2'
    c: Coincident(g16,g6)
    c: Coincident(g16,g5)
    c: Distance(g16,g16) = 57  'fan_spec_screw_spacing'
    c: Coincident(g17,g18)
    c: Coincident(g19,g20)
    c: Perpendicular(g20,g9) = 1.5708
    c: Perpendicular(g19,g11) = 1.5708
    c: Perpendicular(g18,g8) = 4.71239
    c: Perpendicular(g17,g10) = 4.71239
    c: Coincident(g17,g6)
    c: Coincident(g5,g19)
    c: Distance(g18,g18) = 20  'fan_spec_screw1_offset2'
    c: Distance(g17,g17) = 18  'fan_spec_screw1_offset1'
    c: Distance(g19,g19) = 20  'fan_spec_screw2_offset1'
    c: Distance(g20,g20) = 22.4853  'fan_spec_screw2_offset2'
    c: Distance(g4,g0) = 19.5  'fan_spec_opening_width'
    c: Distance(g4,g4) = 2  'fan_spec_opening_depth'
    c: Coincident(g21,g13)
    c: Horizontal(g21)
    c: Coincident(g22,g12)
    c: Horizontal(g22)
    c: Equal(g21,g22)
    c: DistanceX(g15,g15) = 50  'ref_block_width'
    c: DistanceX(g21,g21) = 6  'ref_block_spacing'
    c: Perpendicular(g23,g0) = 4.71239
    c: PointOnObject(g13,g-1)
    c: PointOnObject(g23,g-1)
    c: Coincident(g22,g24)
    c: Coincident(g24,g25)
    c: Coincident(g25,g26)
    c: Coincident(g21,g27)
    c: Coincident(g27,g28)
    c: Coincident(g28,g29)
    c: Equal(g29,g26)
    c: Equal(g28,g25)
    c: Equal(g27,g24)
    c: Equal(g26,g25)
    c: Equal(g28,g27)
    c: Equal(g24,g12)
    c: Vertical(g24)
    c: Vertical(g25)
    c: Vertical(g26)
    c: Vertical(g27)
    c: Vertical(g28)
    c: Vertical(g29)
    c: Symmetric(g4,g0,g23)
    c: Distance(g23,g23) = 22.3813  'duct_flow_length'
    c: DistanceY(g6,g-1) = 35.4187  'screw1_offset_y'
    c: DistanceX(g6,g-1) = 24  'screw1_offset_x'
    c: DistanceY(g5,g-1) = 66.1595  'screw2_offset_y'
    c: DistanceX(g-1,g5) = 24  'screw2_offset_x'
    c: Coincident(g30,g6)
    c: Coincident(g31,g5)
    c: Equal(g30,g31)
    c: Diameter(g31) = 7  'fan_spec_screw_knob'
    c: Horizontal(g32)
    c: PointOnObject(g32,g28)
    c: DistanceX(g32,g32) = 3.5  'screw_knob_clearance'
    c: Perpendicular(g32,g31) = 4.71239
    c: Tangent(g33,g3) = -1.5708
    c: PointOnObject(g33,g16)
    c: Tangent(g34,g1) = -1.5708
    c: PointOnObject(g34,g16)
    c: Distance(g34,g6) = 3.7  'fan_spec_aprox_scroll_intersect1'
    c: PointOnObject(g34,g10)
    c: Distance(g33,g5) = 4.3  'fan_spec_aprox_scroll_intersect2'
    c: Distance(g33,g0) = 28  'fan_spec_aprox_scroll_intersect3'
    c: DistanceY(g7,g-1) = 50  'fan_center_offset'
    c: Coincident(g36,g4)
    c: Coincident(g35,g0)
    c: PointOnObject(g35,g-1)
    c: PointOnObject(g36,g-1)
    c: Parallel(g23,g35)
    c: Parallel(g23,g36)
    c: Angle(g-1,g0) = 0.160106  'fan_angle'
    c: Coincident(g37,g6)
    c: Coincident(g38,g5)
    c: Equal(g37,g38)
    c: Diameter(g37) = 4  'fan_screw_insert'
    c: DistanceY(g0,g-1) = 20.5407  'fan_corner_offset_y'
    c: DistanceX(g-1,g0) = 21.7128  'fan_corner_offset_x'
    c: Coincident(g39,g40)
    c: Coincident(g40,g41)
    c: Coincident(g41,g42)
    c: Coincident(g42,g39)
    c: Vertical(g39)
    c: Vertical(g41)
    c: Horizontal(g40)
    c: Symmetric(g41,g39,g-2)
    c: PointOnObject(g39,g-1)
    c: DistanceY(g41,g41) = 80  'base_length'
    c: DistanceX(g40,g40) = 62  'base_width'
    c: Coincident(g43,g44)
    c: Coincident(g45,g43)
    c: Vertical(g43)
    c: Horizontal(g44)
    c: Horizontal(g45)
    c: Coincident(g45,g46)
    c: Vertical(g46)
    c: Coincident(g46,g47)
    c: Vertical(g47)
    c: Coincident(g47,g48)
    c: Coincident(g48,g44)
    c: Vertical(g48)
    c: Coincident(g49,g50)
    c: Vertical(g50)
    c: Coincident(g50,g51)
    c: Vertical(g51)
    c: Coincident(g51,g52)
    c: Horizontal(g52)
    c: Coincident(g52,g53)
    c: Vertical(g53)
    c: Coincident(g53,g54)
    c: Coincident(g54,g49)
    c: Horizontal(g54)
    c: Equal(g48,g47)
    c: Equal(g47,g46)
    c: Equal(g51,g50)
    c: Equal(g50,g49)
    c: Equal(g50,g47)
    c: Coincident(g55,g56)
    c: Coincident(g56,g57)
    c: Coincident(g57,g58)
    c: Coincident(g58,g55)
    c: Vertical(g57)
    c: Horizontal(g56)
    c: Horizontal(g58)
    c: Coincident(g55,g46)
    c: Coincident(g59,g60)
    c: Coincident(g60,g61)
    c: Coincident(g61,g62)
    c: Coincident(g62,g59)
    c: Horizontal(g59)
    c: Horizontal(g61)
    c: Vertical(g60)
    c: Coincident(g59,g49)
    c: Coincident(g61,g50)
    c: Coincident(g55,g47)
    c: Equal(g58,g59)
    c: Equal(g54,g45)
    c: Vertical(g49)
    c: Distance(g45,g45) = 3  'estimated_side_thickness'
    c: Distance(g58,g58) = 2.8  'estimated_screw_head_height'
    c: DistanceY(g57,g57) = 5.6  'estimated_screw_head_width'
    c: PointOnObject(g64,g47)
    c: PointOnObject(g63,g51)
    c: Symmetric(g50,g49,g63)
    c: Symmetric(g46,g47,g64)
    c: PointOnObject(g63,g53)
    c: PointOnObject(g64,g43)
    c: PointOnObject(g43,g39)
    c: PointOnObject(g53,g41)
    c: DistanceY(g63,g-1) = 28  'estimated_side_screw_offset_right'
    c: DistanceY(g64,g-1) = 28  'estimated_side_screw_offset_left'
FEATURE [PartDesign::Pad] Pad  label="hfd_base"
  Direction = (0,0,1)
  Length = 3
  Length2 = 10
  Profile = -> Sketch
  ReferenceAxis = -> Sketch [N_Axis]
  Refine = true
  Reversed = true
  SideType = 0
  Suppressed = false
  Type = 0
  Type2 = 0
FEATURE [Sketcher::SketchObject] Sketch089  label="hfd_side_s"
  ArcFitTolerance = 1e-06
  AttachmentSupport = -> [XZ_Plane140]
  ExternalTypes = [0]
  FullyConstrained = true
  MakeInternals = false
  MapMode = 5
  Placement = pos=(0,0,0) rot=(1,0,0;1.5708rad)
  _ExternalGeoVersion = 0
  expr: .Constraints.base_thickness = <<hfd_base>>.Length
  expr: .Constraints.base_width = <<hfd_base_s>>.Constraints.base_width
  expr: .Constraints.duct_edge = <<bracket_params>>.feature_block_offset
  sketch-geometry (31):
    g0: LineSegment StartX=-31 StartY=0 StartZ=0 EndX=-28 EndY=0 EndZ=0
    g1: LineSegment StartX=-28 StartY=0 StartZ=0 EndX=-28 EndY=13 EndZ=0
    g2: LineSegment StartX=-28 StartY=13 StartZ=0 EndX=-31 EndY=13 EndZ=0
    g3: LineSegment [constr] StartX=-31 StartY=9 StartZ=0 EndX=-32 EndY=9 EndZ=0
    g4: LineSegment [constr] StartX=-32 StartY=9 StartZ=0 EndX=-32 EndY=3 EndZ=0
    g5: LineSegment [constr] StartX=-32 StartY=3 StartZ=0 EndX=-31 EndY=3 EndZ=0
    g6: LineSegment StartX=31 StartY=0 StartZ=0 EndX=28 EndY=0 EndZ=0
    g7: LineSegment StartX=28 StartY=0 StartZ=0 EndX=28 EndY=13 EndZ=0
    g8: LineSegment StartX=28 StartY=13 StartZ=0 EndX=31 EndY=13 EndZ=0
    g9: LineSegment [constr] StartX=31 StartY=9 StartZ=0 EndX=32 EndY=9 EndZ=0
    g10: LineSegment [constr] StartX=32 StartY=9 StartZ=0 EndX=32 EndY=3 EndZ=0
    g11: LineSegment [constr] StartX=32 StartY=3 StartZ=0 EndX=31 EndY=3 EndZ=0
    g12: LineSegment [constr] StartX=-28 StartY=13 StartZ=0 EndX=28 EndY=13 EndZ=0
    g13: LineSegment [constr] StartX=-31 StartY=9 StartZ=0 EndX=31 EndY=9 EndZ=0
    g14: LineSegment [constr] StartX=-31 StartY=3 StartZ=0 EndX=31 EndY=3 EndZ=0
    g15: LineSegment [constr] StartX=-32 StartY=6 StartZ=0 EndX=-31 EndY=6 EndZ=0
    g16: LineSegment [constr] StartX=-31 StartY=6 StartZ=0 EndX=0 EndY=6 EndZ=0
    g17: LineSegment [constr] StartX=0 StartY=6 StartZ=0 EndX=31 EndY=6 EndZ=0
    g18: LineSegment [constr] StartX=31 StartY=6 StartZ=0 EndX=32 EndY=6 EndZ=0
    g19: LineSegment [constr] StartX=-10 StartY=16 StartZ=0 EndX=-10 EndY=-4 EndZ=0
    g20: LineSegment [constr] StartX=-10 StartY=-4 StartZ=0 EndX=10 EndY=-4 EndZ=0
    g21: LineSegment [constr] StartX=10 StartY=-4 StartZ=0 EndX=10 EndY=16 EndZ=0
    g22: LineSegment [constr] StartX=10 StartY=16 StartZ=0 EndX=-10 EndY=16 EndZ=0
    g23: Circle [constr] CenterX=0 CenterY=6 CenterZ=0 NormalX=0 NormalY=0 NormalZ=1 AngleXU=0 Radius=10
    g24: LineSegment [constr] StartX=-28 StartY=0 StartZ=0 EndX=-28 EndY=-3 EndZ=0
    g25: LineSegment [constr] StartX=0 StartY=15 StartZ=0 EndX=28 EndY=15 EndZ=0
    g26: LineSegment [constr] StartX=0 StartY=16.2 StartZ=0 EndX=28 EndY=16.2 EndZ=0
    g27: LineSegment [constr] StartX=25 StartY=16.2 StartZ=0 EndX=25 EndY=13 EndZ=0
    g28: LineSegment [constr] StartX=25.4 StartY=16.2 StartZ=0 EndX=28 EndY=13.6 EndZ=0
    g29: LineSegment StartX=-31 StartY=0 StartZ=0 EndX=-31 EndY=13 EndZ=0
    g30: LineSegment StartX=31 StartY=13 StartZ=0 EndX=31 EndY=0 EndZ=0
  constraints (99):
    c: Coincident(g0,g1)
    c: Vertical(g1)
    c: Coincident(g1,g2)
    c: Coincident(g3,g4)
    c: Coincident(g4,g5)
    c: Coincident(g6,g7)
    c: Vertical(g7)
    c: Coincident(g7,g8)
    c: Horizontal(g8)
    c: Coincident(g9,g10)
    c: Coincident(g10,g11)
    c: Coincident(g12,g1)
    c: Coincident(g12,g7)
    c: Horizontal(g12)
    c: Horizontal(g13)
    c: Coincident(g14,g5)
    c: Horizontal(g14)
    c: Vertical(g4)
    c: Horizontal(g2)
    c: Vertical(g10)
    c: PointOnObject(g6,g-1)
    c: PointOnObject(g0,g-1)
    c: PointOnObject(g0,g-1)
    c: Equal(g2,g8)
    c: Symmetric(g0,g6,g-2)
    c: DistanceX(g2,g8) = 62  'base_width'
    c: Distance(g2,g2) = 3  'side_width'
    c: Horizontal(g15)
    c: Coincident(g15,g16)
    c: Horizontal(g16)
    c: Coincident(g16,g17)
    c: Horizontal(g17)
    c: Coincident(g17,g18)
    c: Equal(g15,g18)
    c: Equal(g17,g16)
    c: PointOnObject(g16,g-2)
    c: PointOnObject(g15,g4)
    c: PointOnObject(g18,g10)
    c: Symmetric(g10,g9,g18)
    c: Horizontal(g9)
    c: Horizontal(g11)
    c: Horizontal(g3)
    c: Horizontal(g5)
    c: DistanceY(g4,g4) = 6  'tab_width'
    c: Coincident(g19,g20)
    c: Coincident(g20,g21)
    c: Coincident(g21,g22)
    c: Coincident(g22,g19)
    c: Vertical(g19)
    c: Vertical(g21)
    c: Horizontal(g20)
    c: Horizontal(g22)
    c: Tangent(g23,g22)
    c: Tangent(g23,g19)
    c: Tangent(g23,g20)
    c: Tangent(g23,g21)
    c: DistanceX(g22,g22) = 20  'extrusion_width'
    c: Coincident(g23,g16)
    c: Coincident(g24,g0)
    c: DistanceY(g24,g24) = 3  'base_thickness'
    c: DistanceY(g19,g24) = 1  'base_rise'
    c: Distance(g3,g3) = 1  'tab_depth'
    c: DistanceY(g1,g19) = 3  'side_recess'
    c: DistanceY(g0,g5) = 3  'height_side_to_tab'
    c: DistanceY(g24,g4) = 6  'height_base_to_tab'
    c: Distance(g2,g3) = 4  'height_side_above_tab'
    c: Vertical(g24)
    c: DistanceY(g24,g7) = 16  'side_height'
    c: Horizontal(g25)
    c: Horizontal(g26)
    c: PointOnObject(g25,g7)
    c: PointOnObject(g26,g7)
    c: PointOnObject(g25,g-2)
    c: PointOnObject(g26,g-2)
    c: DistanceY(g-1,g25) = 15  'fan_top'
    c: DistanceY(g25,g26) = 1.2  'estimate_duct_thick'
    c: PointOnObject(g27,g26)
    c: PointOnObject(g27,g12)
    c: Vertical(g27)
    c: DistanceX(g27,g8) = 6  'duct_edge'
    c: PointOnObject(g28,g26)
    c: PointOnObject(g28,g7)
    c: Angle(g28,g26) = 0.785398  'estimate_duct_chmf_angle'
    c: Distance(g26,g28) = 2.6  'estimate_duct_chmf'
    c: Coincident(g29,g0)
    c: Coincident(g29,g2)
    c: Vertical(g29)
    c: Coincident(g3,g13)
    c: Coincident(g9,g13)
    c: Coincident(g11,g14)
    c: Coincident(g30,g8)
    c: Coincident(g30,g6)
    c: Vertical(g30)
    c: PointOnObject(g3,g29)
    c: PointOnObject(g15,g29)
    c: PointOnObject(g5,g29)
    c: PointOnObject(g9,g30)
    c: PointOnObject(g11,g30)
    c: Distance(g-1,g16) = 6  'tab_plane'
FEATURE [PartDesign::Pad] Pad023  label="hfd_side"
  BaseFeature = -> Pad
  Direction = (0,-1,2e-16)
  Length = 80
  Length2 = 10
  Profile = -> Sketch089
  ReferenceAxis = -> Sketch089 [N_Axis]
  Refine = true
  SideType = 0
  Suppressed = false
  Type = 0
  Type2 = 0
  expr: Length = <<hfd_base_s>>.Constraints.base_length
FEATURE [Sketcher::SketchObject] Sketch090  label="hfd_side_tabs_s"
  ArcFitTolerance = 1e-06
  AttachmentOffset = pos=(0,0,6) rot=(0,0,1;0rad)
  AttachmentSupport = -> [XY_Plane140]
  ExternalTypes = [0]
  FullyConstrained = true
  MakeInternals = false
  MapMode = 5
  Placement = pos=(0,0,6) rot=(0,0,1;0rad)
  _ExternalGeoVersion = 0
  expr: .AttachmentOffset.Base.z = <<hfd_side_s>>.Constraints.tab_plane
  expr: .Constraints.base_length = <<hfd_base_s>>.Constraints.base_length
  expr: .Constraints.base_width = <<hfd_base_s>>.Constraints.base_width
  sketch-geometry (29):
    g0: LineSegment StartX=-32 StartY=-7 StartZ=0 EndX=-32 EndY=-23 EndZ=0
    g1: LineSegment StartX=-32 StartY=-23 StartZ=0 EndX=-31 EndY=-23 EndZ=0
    g2: LineSegment StartX=-31 StartY=-23 StartZ=0 EndX=-31 EndY=-7 EndZ=0
    g3: LineSegment StartX=-31 StartY=-7 StartZ=0 EndX=-32 EndY=-7 EndZ=0
    g4: LineSegment StartX=-32 StartY=-39 StartZ=0 EndX=-32 EndY=-73 EndZ=0
    g5: LineSegment StartX=-32 StartY=-73 StartZ=0 EndX=-31 EndY=-73 EndZ=0
    g6: LineSegment StartX=-31 StartY=-73 StartZ=0 EndX=-31 EndY=-39 EndZ=0
    g7: LineSegment StartX=-31 StartY=-39 StartZ=0 EndX=-32 EndY=-39 EndZ=0
    g8: LineSegment StartX=31 StartY=-7 StartZ=0 EndX=31 EndY=-23 EndZ=0
    g9: LineSegment StartX=31 StartY=-23 StartZ=0 EndX=32 EndY=-23 EndZ=0
    g10: LineSegment StartX=32 StartY=-23 StartZ=0 EndX=32 EndY=-7 EndZ=0
    g11: LineSegment StartX=32 StartY=-7 StartZ=0 EndX=31 EndY=-7 EndZ=0
    g12: LineSegment StartX=31 StartY=-40.5 StartZ=0 EndX=31 EndY=-73 EndZ=0
    g13: LineSegment StartX=31 StartY=-73 StartZ=0 EndX=32 EndY=-73 EndZ=0
    g14: LineSegment StartX=32 StartY=-73 StartZ=0 EndX=32 EndY=-40.5 EndZ=0
    g15: LineSegment StartX=32 StartY=-40.5 StartZ=0 EndX=31 EndY=-40.5 EndZ=0
    g16: LineSegment [constr] StartX=-31 StartY=-23 StartZ=0 EndX=-31 EndY=-39 EndZ=0
    g17: LineSegment [constr] StartX=31 StartY=-23 StartZ=0 EndX=31 EndY=-40.5 EndZ=0
    g18: LineSegment [constr] StartX=31 StartY=-73 StartZ=0 EndX=31 EndY=-80 EndZ=0
    g19: LineSegment [constr] StartX=31 StartY=-80 StartZ=0 EndX=-31 EndY=-80 EndZ=0
    g20: LineSegment [constr] StartX=-31 StartY=-80 StartZ=0 EndX=-31 EndY=-73 EndZ=0
    g21: LineSegment [constr] StartX=-31 StartY=-7 StartZ=0 EndX=-31 EndY=0 EndZ=0
    g22: LineSegment [constr] StartX=31 StartY=-7 StartZ=0 EndX=31 EndY=0 EndZ=0
    g23: LineSegment [constr] StartX=0 StartY=-28 StartZ=0 EndX=-32 EndY=-28 EndZ=0
    g24: LineSegment [constr] StartX=0 StartY=-28 StartZ=0 EndX=32 EndY=-28 EndZ=0
    g25: LineSegment [constr] StartX=32 StartY=-23 StartZ=0 EndX=32 EndY=-28 EndZ=0
    g26: LineSegment [constr] StartX=32 StartY=-28 StartZ=0 EndX=32 EndY=-40.5 EndZ=0
    g27: LineSegment [constr] StartX=-32 StartY=-23 StartZ=0 EndX=-32 EndY=-28 EndZ=0
    g28: LineSegment [constr] StartX=-32 StartY=-28 StartZ=0 EndX=-32 EndY=-39 EndZ=0
  constraints (85):
    c: Coincident(g0,g1)
    c: Coincident(g1,g2)
    c: Coincident(g2,g3)
    c: Coincident(g3,g0)
    c: Vertical(g0)
    c: Vertical(g2)
    c: Horizontal(g1)
    c: Horizontal(g3)
    c: Coincident(g4,g5)
    c: Coincident(g5,g6)
    c: Coincident(g6,g7)
    c: Coincident(g7,g4)
    c: Vertical(g4)
    c: Vertical(g6)
    c: Horizontal(g5)
    c: Horizontal(g7)
    c: Coincident(g8,g9)
    c: Coincident(g9,g10)
    c: Coincident(g10,g11)
    c: Coincident(g11,g8)
    c: Vertical(g8)
    c: Vertical(g10)
    c: Horizontal(g9)
    c: Horizontal(g11)
    c: Coincident(g12,g13)
    c: Coincident(g13,g14)
    c: Coincident(g14,g15)
    c: Coincident(g15,g12)
    c: Vertical(g12)
    c: Vertical(g14)
    c: Horizontal(g13)
    c: Horizontal(g15)
    c: Coincident(g16,g1)
    c: Coincident(g16,g6)
    c: Coincident(g17,g8)
    c: Coincident(g17,g12)
    c: Vertical(g17)
    c: Coincident(g18,g12)
    c: Coincident(g19,g18)
    c: Horizontal(g19)
    c: Coincident(g20,g19)
    c: Coincident(g20,g5)
    c: Coincident(g21,g2)
    c: PointOnObject(g21,g-1)
    c: Coincident(g22,g8)
    c: Vertical(g21)
    c: Vertical(g22)
    c: Vertical(g16)
    c: Vertical(g20)
    c: Vertical(g18)
    c: Equal(g1,g9)
    c: Equal(g9,g15)
    c: Equal(g15,g7)
    c: Distance(g3,g3) = 1  'tab_depth'
    c: Symmetric(g21,g22,g-2)
    c: DistanceX(g21,g22) = 62  'base_width'
    c: DistanceY(g18,g-1) = 80  'base_length'
    c: Equal(g20,g18)
    c: Equal(g21,g22)
    c: DistanceY(g21,g21) = 7  'end_offset1'
    c: DistanceY(g20,g20) = 7  'end_offset2'
    c: PointOnObject(g23,g-2)
    c: PointOnObject(g24,g-2)
    c: Coincident(g25,g9)
    c: Coincident(g26,g25)
    c: Coincident(g26,g14)
    c: Coincident(g27,g0)
    c: Coincident(g28,g27)
    c: Coincident(g28,g4)
    c: Vertical(g27)
    c: Vertical(g25)
    c: Coincident(g24,g25)
    c: Coincident(g23,g27)
    c: Horizontal(g24)
    c: Horizontal(g23)
    c: DistanceY(g10,g10) = 16  'tab1_right'
    c: DistanceY(g0,g0) = 16  'tab1_left'
    c: DistanceY(g4,g4) = 34  'tab2_left'
    c: DistanceY(g14,g14) = 32.5  'tab2_right'
    c: DistanceY(g23,g-1) = 28  'screw_placement_left'
    c: DistanceY(g24,g-1) = 28  'screw_placement_right'
    c: DistanceY(g27,g27) = 5  'nut_clear_left_front'
    c: Distance(g25,g25) = 5  'nut_clear_right_front'
    c: Distance(g28,g28) = 11  'nut_clear_left_rear'
    c: Distance(g26,g26) = 12.5  'nut_clear_right_rear'
FEATURE [PartDesign::Pad] Pad024  label="hfd_side_tabs"
  BaseFeature = -> Pad023
  Direction = (0,0,1)
  Length = 6
  Length2 = 10
  Profile = -> Sketch090
  ReferenceAxis = -> Sketch090 [N_Axis]
  Refine = true
  SideType = 0
  Suppressed = false
  Type = 0
  Type2 = 0
  expr: Length = <<hfd_side_s>>.Constraints.tab_width
FEATURE [PartDesign::Chamfer] Chamfer  label="hfd_side_tab_chmf"
  Angle = 45
  Base = -> Pad024 [Edge67,Edge70,Edge75,Edge78,Edge58,Edge62,Edge50,Edge54]
  BaseFeature = -> Pad024
  ChamferType = 0
  FlipDirection = false
  Refine = true
  Size = 0.6
  Size2 = 1
  SupportTransform = false
  Suppressed = false
  UseAllEdges = false
FEATURE [PartDesign::Fillet] Fillet016  label="hfd_side_tab_flt"
  Base = -> Chamfer [Edge82,Edge7,Edge1,Edge52,Edge45,Edge94,Edge87,Edge75]
  BaseFeature = -> Chamfer
  Radius = 0.8
  Refine = true
  SupportTransform = false
  Suppressed = false
  UseAllEdges = false
FEATURE [Sketcher::SketchObject] Sketch091  label="hfd_side_screw_left_s"
  ArcFitTolerance = 1e-06
  AttachmentSupport = -> [YZ_Plane140]
  ExternalTypes = [0]
  FullyConstrained = true
  MakeInternals = false
  MapMode = 5
  Placement = pos=(0,0,0) rot=(0.57735,0.57735,0.57735;2.0944rad)
  _ExternalGeoVersion = 0
  expr: .Constraints.screw_height = <<hfd_side_s>>.Constraints.tab_plane
  expr: .Constraints.screw_offset = <<hfd_side_tabs_s>>.Constraints.screw_placement_left
  sketch-geometry (2):
    g0: Circle CenterX=-28 CenterY=6 CenterZ=0 NormalX=0 NormalY=0 NormalZ=1 AngleXU=0 Radius=1.7
    g1: Circle [constr] CenterX=-28 CenterY=6 CenterZ=0 NormalX=0 NormalY=0 NormalZ=1 AngleXU=0 Radius=2.8
  constraints (5):
    c: Coincident(g1,g0)
    c: Diameter(g0) = 3.4  'hole_diam'
    c: Diameter(g1) = 5.6  'screw_head'
    c: DistanceY(g-1,g0) = 6  'screw_height'
    c: DistanceX(g0,g-1) = 28  'screw_offset'
FEATURE [PartDesign::Pocket] Pocket031  label="hfd_side_screw_left"
  BaseFeature = -> Fillet016
  Direction = (-1,0,0)
  Length = 5
  Length2 = 5
  Profile = -> Sketch091
  ReferenceAxis = -> Sketch091 [N_Axis]
  Refine = true
  SideType = 0
  Suppressed = false
  Type = 1
  Type2 = 0
FEATURE [Sketcher::SketchObject] Sketch092  label="hfd_side_screw_right_s"
  ArcFitTolerance = 1e-06
  AttachmentSupport = -> [YZ_Plane140]
  ExternalTypes = [0]
  FullyConstrained = true
  MakeInternals = false
  MapMode = 5
  Placement = pos=(0,0,0) rot=(0.57735,0.57735,0.57735;2.0944rad)
  _ExternalGeoVersion = 0
  expr: .Constraints.hole_diam = <<hfd_side_screw_left_s>>.Constraints.hole_diam
  expr: .Constraints.screw_head = <<hfd_side_screw_left_s>>.Constraints.screw_head
  expr: .Constraints.screw_height = <<hfd_side_s>>.Constraints.tab_plane
  expr: .Constraints.screw_offset = <<hfd_side_tabs_s>>.Constraints.screw_placement_right
  sketch-geometry (2):
    g0: Circle CenterX=-28 CenterY=6 CenterZ=0 NormalX=0 NormalY=0 NormalZ=1 AngleXU=0 Radius=1.7
    g1: Circle [constr] CenterX=-28 CenterY=6 CenterZ=0 NormalX=0 NormalY=0 NormalZ=1 AngleXU=0 Radius=2.8
  constraints (5):
    c: Coincident(g1,g0)
    c: Diameter(g0) = 3.4  'hole_diam'
    c: Diameter(g1) = 5.6  'screw_head'
    c: DistanceY(g-1,g0) = 6  'screw_height'
    c: DistanceX(g0,g-1) = 28  'screw_offset'
FEATURE [PartDesign::Pocket] Pocket032  label="hfd_side_screw_right"
  BaseFeature = -> Pocket031
  Direction = (-1,0,0)
  Length = 5
  Length2 = 5
  Profile = -> Sketch092
  ReferenceAxis = -> Sketch092 [N_Axis]
  Refine = true
  Reversed = true
  SideType = 0
  Suppressed = false
  Type = 1
  Type2 = 0
FEATURE [Sketcher::SketchObject] Sketch093  label="hfd_duct_wall_s"
  ArcFitTolerance = 1e-06
  AttachmentSupport = -> [XY_Plane140]
  ExternalTypes = [0]
  FullyConstrained = false
  MakeInternals = false
  MapMode = 5
  _ExternalGeoVersion = 0
  expr: .Constraints.block_width = <<hfd_base_s>>.Constraints.ref_block_width
  expr: .Constraints.fan_angle = <<hfd_base_s>>.Constraints.fan_angle
  expr: .Constraints.fan_corner_x = <<hfd_base_s>>.Constraints.fan_corner_offset_x
  expr: .Constraints.fan_corner_y = <<hfd_base_s>>.Constraints.fan_corner_offset_y
  expr: .Constraints.fan_open_depth = <<hfd_base_s>>.Constraints.fan_spec_opening_depth
  expr: .Constraints.fan_opening = <<hfd_base_s>>.Constraints.fan_spec_opening_width
  expr: .Constraints.inner_width = <<hfd_side_s>>.Constraints.base_width - 2 * <<hfd_side_s>>.Constraints.side_width
  sketch-geometry (40):
    g0: LineSegment [constr] StartX=2.46216 StartY=-23.6495 StartZ=0 EndX=2.781 EndY=-25.6239 EndZ=0
    g1: LineSegment [constr] StartX=2.781 StartY=-25.6239 StartZ=0 EndX=22.0316 EndY=-22.5151 EndZ=0
    g2: LineSegment [constr] StartX=22.0316 StartY=-22.5151 StartZ=0 EndX=21.7128 EndY=-20.5407 EndZ=0
    g3: LineSegment [constr] StartX=21.7128 StartY=-20.5407 StartZ=0 EndX=2.46216 EndY=-23.6495 EndZ=0
    g4: LineSegment [constr] StartX=-25 StartY=0 StartZ=0 EndX=25 EndY=0 EndZ=0
    g5: LineSegment StartX=21.8495 StartY=-19.5057 StartZ=0 EndX=22.3278 EndY=-22.4673 EndZ=0
    g6: LineSegment StartX=23.6 StartY=0 StartZ=0 EndX=23.6 EndY=-1 EndZ=0
    g7: LineSegment StartX=-23.6 StartY=0 StartZ=0 EndX=-23.6 EndY=-1 EndZ=0
    g8: LineSegment [constr] StartX=-25 StartY=0 StartZ=0 EndX=-23.6 EndY=0 EndZ=0
    g9: LineSegment [constr] StartX=25 StartY=0 StartZ=0 EndX=23.6 EndY=0 EndZ=0
    g10: LineSegment [constr] StartX=21.7128 StartY=-20.5407 StartZ=0 EndX=22.0089 EndY=-20.4929 EndZ=0
    g11: LineSegment [constr] StartX=2.46216 StartY=-23.6495 StartZ=0 EndX=2.16599 EndY=-23.6973 EndZ=0
    g12: LineSegment [constr] StartX=2.48484 StartY=-25.6717 StartZ=0 EndX=22.3278 EndY=-22.4673 EndZ=0
    g13: LineSegment StartX=2.48484 StartY=-25.6717 StartZ=0 EndX=2.00657 EndY=-22.7101 EndZ=0
    g14: LineSegment [constr] StartX=2.00657 StartY=-22.7101 StartZ=0 EndX=21.8495 EndY=-19.5057 EndZ=0
    g15-g18: Circle [constr] x4 (B-spline internal-alignment scaffolding for g19; pole/knot coordinates omitted)
    g19: BSplineCurve PolesCount=4 KnotsCount=2 Degree=3 IsPeriodic=0
    g20: GeomPoint [constr] X=21.8495 Y=-19.5057 Z=0
    g21: GeomPoint [constr] X=23.6 Y=-1 Z=0
    g22-g25: Circle [constr] x4 (B-spline internal-alignment scaffolding for g26; pole/knot coordinates omitted)
    g26: BSplineCurve PolesCount=4 KnotsCount=2 Degree=3 IsPeriodic=0
    g27: GeomPoint [constr] X=2.00657 Y=-22.7101 Z=0
    g28: GeomPoint [constr] X=-23.6 Y=-1 Z=0
    g29: LineSegment StartX=28 StartY=0 StartZ=0 EndX=23.6 EndY=0 EndZ=0
    g30: LineSegment StartX=-23.6 StartY=0 StartZ=0 EndX=-28 EndY=0 EndZ=0
    g31: LineSegment StartX=28 StartY=0 StartZ=0 EndX=28 EndY=-18.4956 EndZ=0
    g32: LineSegment StartX=2.48484 StartY=-25.6717 StartZ=0 EndX=-22.3278 EndY=-22.4673 EndZ=0
    g33: LineSegment StartX=22.3278 StartY=-22.4673 StartZ=0 EndX=28 EndY=-18.4956 EndZ=0
    g34: LineSegment [constr] StartX=28 StartY=-18.4956 StartZ=0 EndX=28 EndY=-21.5513 EndZ=0
    g35: LineSegment [constr] StartX=-28 StartY=-18.4956 StartZ=0 EndX=28 EndY=-18.4956 EndZ=0
    g36: LineSegment StartX=-28 StartY=0 StartZ=0 EndX=-28 EndY=-18.4956 EndZ=0
    g37: LineSegment StartX=-28 StartY=-18.4956 StartZ=0 EndX=-22.3278 EndY=-22.4673 EndZ=0
    g38: LineSegment [constr] StartX=-28 StartY=-18.4956 StartZ=0 EndX=-28 EndY=-21.5513 EndZ=0
    g39: LineSegment [constr] StartX=-22.3278 StartY=-22.4673 StartZ=0 EndX=22.3278 EndY=-22.4673 EndZ=0
  constraints (92):
    c: Coincident(g0,g1)
    c: Coincident(g1,g2)
    c: Coincident(g2,g3)
    c: Coincident(g3,g0)
    c: DistanceY(g2,g-1) = 20.5407  'fan_corner_y'
    c: DistanceX(g-1,g2) = 21.7128  'fan_corner_x'
    c: Angle(g-1,g3) = 0.160106  'fan_angle'
    c: Distance(g3,g3) = 19.5  'fan_opening'
    c: Perpendicular(g3,g0)
    c: Perpendicular(g3,g2)
    c: Parallel(g1,g3)
    c: Distance(g0,g0) = 2  'fan_open_depth'
    c: Symmetric(g4,g4,g-2)
    c: DistanceX(g4,g4) = 50  'block_width'
    c: PointOnObject(g4,g-1)
    c: Equal(g8,g9)
    c: Coincident(g8,g4)
    c: Coincident(g7,g8)
    c: Coincident(g9,g4)
    c: Coincident(g6,g9)
    c: Equal(g7,g6)
    c: Distance(g8,g8) = 1.4  'block_inset'
    c: PointOnObject(g7,g-1)
    c: PointOnObject(g6,g-1)
    c: Vertical(g7)
    c: Vertical(g6)
    c: Distance(g7,g7) = 1  'duct_final_straight'
    c: Perpendicular(g3,g5)
    c: Coincident(g10,g2)
    c: PointOnObject(g10,g5)
    c: Coincident(g11,g0)
    c: Equal(g11,g10)
    c: Parallel(g11,g3)
    c: Parallel(g3,g10)
    c: Coincident(g12,g5)
    c: Parallel(g12,g3)
    c: Distance(g10,g10) = 0.3  'fan_clear'
    c: Distance(g11,g12) = 2  'fan_overlap'
    c: Coincident(g13,g12)
    c: PointOnObject(g11,g13)
    c: Perpendicular(g3,g13)
    c: Coincident(g14,g13)
    c: Coincident(g14,g5)
    c: Parallel(g14,g3)
    c: Distance(g11,g13) = 1  'start_straight'
    c: Weight(g15) = 1
    c: Equal(g15,g16)
    c: Equal(g15,g17)
    c: Equal(g15,g18)
    c: InternalAlignment(g15-g18 -> g19) x4
    c: InternalAlignment(g20,g19)
    c: InternalAlignment(g21,g19)
    c: Weight(g22) = 1
    c: Equal(g22,g23)
    c: Equal(g22,g24)
    c: Equal(g22,g25)
    c: InternalAlignment(g22-g25 -> g26) x4
    c: InternalAlignment(g27,g26)
    c: InternalAlignment(g28,g26)
    c: Tangent(g19,g6) = 1.5708
    c: Tangent(g26,g7) = 1.5708
    c: Tangent(g26,g13) = -1.5708
    c: Tangent(g19,g5) = 1.5708
    c: Coincident(g31,g29)
    c: Coincident(g6,g29)
    c: Coincident(g30,g7)
    c: Equal(g30,g29)
    c: PointOnObject(g29,g-1)
    c: PointOnObject(g30,g-1)
    c: DistanceX(g30,g29) = 56  'inner_width'
    c: Vertical(g31)
    c: Coincident(g32,g12)
    c: Coincident(g33,g5)
    c: Coincident(g33,g31)
    c: Coincident(g34,g31)
    c: Parallel(g34,g31)
    c: PointOnObject(g34,g1)
    c: Angle(g33,g34) = 0.959931  'back_angle_wall_right'
    c: Horizontal(g35)
    c: Coincident(g35,g31)
    c: Coincident(g30,g36)
    c: Vertical(g36)
    c: Coincident(g36,g37)
    c: Coincident(g37,g32)
    c: Coincident(g35,g36)
    c: Coincident(g38,g35)
    c: Vertical(g38)
    c: Angle(g38,g37) = 0.959931  'back_angle_wall_left'
    c: Equal(g34,g38)
    c: Horizontal(g39)
    c: Coincident(g39,g32)
    c: Coincident(g39,g5)
FEATURE [PartDesign::Pad] Pad025  label="hfd_duct_wall"
  BaseFeature = -> Pocket032
  Direction = (0,0,1)
  Length = 15.2
  Length2 = 10
  Profile = -> Sketch093
  ReferenceAxis = -> Sketch093 [N_Axis]
  Refine = true
  SideType = 0
  Suppressed = false
  Type = 0
  Type2 = 0
FEATURE [Sketcher::SketchObject] Sketch094  label="hfd_duct_top_s"
  ArcFitTolerance = 1e-06
  AttachmentSupport = -> [Pad025]
  ExternalGeometry = -> [Pad025]
  ExternalTypes = [0]
  FullyConstrained = true
  MakeInternals = false
  MapMode = 5
  Placement = pos=(0,0,15.2) rot=(0,0,1;0rad)
  _ExternalGeoVersion = 0
  expr: .Constraints.base_rise = <<hfd_side_s>>.Constraints.base_rise
  expr: .Constraints.depth_base = <<hfd_base>>.Length
  expr: .Constraints.depth_duct_side = <<hfd_duct_wall>>.Length
  sketch-geometry (14):
    g0: LineSegment StartX=-28 StartY=0 StartZ=0 EndX=28 EndY=0 EndZ=0
    g1: LineSegment StartX=28 StartY=0 StartZ=0 EndX=28 EndY=-18.4956 EndZ=0
    g2: LineSegment StartX=28 StartY=-18.4956 StartZ=0 EndX=22.3278 EndY=-22.4673 EndZ=0
    g3: LineSegment StartX=22.3278 StartY=-22.4673 StartZ=0 EndX=2.48484 EndY=-25.6717 EndZ=0
    g4: LineSegment StartX=-28 StartY=0 StartZ=0 EndX=-28 EndY=-18.4956 EndZ=0
    g5: LineSegment StartX=-28 StartY=-18.4956 StartZ=0 EndX=-22.3278 EndY=-22.4673 EndZ=0
    g6: LineSegment StartX=-22.3278 StartY=-22.4673 StartZ=0 EndX=2.48484 EndY=-25.6717 EndZ=0
    g7: GeomPoint [constr] X=0 Y=1 Z=0
    g8: GeomPoint [constr] X=0 Y=4 Z=0
    g9: GeomPoint [constr] X=0 Y=19.2 Z=0
    g10: GeomPoint [constr] X=0 Y=22 Z=0
    g11: GeomPoint [constr] X=0 Y=2.5 Z=0
    g12: GeomPoint [constr] X=0 Y=22.5 Z=0
    g13: GeomPoint [constr] X=0 Y=19.6 Z=0
  constraints (29):
    c: Coincident(g0,g-5)
    c: Coincident(g0,g1)
    c: Coincident(g1,g-4)
    c: Coincident(g1,g2)
    c: Coincident(g2,g-3)
    c: Coincident(g2,g3)
    c: Coincident(g3,g-7)
    c: Coincident(g4,g0)
    c: Coincident(g4,g-9)
    c: Coincident(g5,g4)
    c: Coincident(g5,g-8)
    c: Coincident(g6,g5)
    c: Coincident(g6,g3)
    c: Coincident(g0,g-6)
    c: PointOnObject(g7,g-2)
    c: PointOnObject(g8,g-2)
    c: PointOnObject(g9,g-2)
    c: PointOnObject(g10,g-2)
    c: Distance(g-1,g7) = 1  'base_rise'
    c: DistanceY(g7,g8) = 3  'depth_base'
    c: DistanceY(g8,g9) = 15.2  'depth_duct_side'
    c: Distance(g9,g10) = 2.8  'extrude'
    c: PointOnObject(g11,g-2)
    c: PointOnObject(g12,g-2)
    c: DistanceY(g11,g12) = 20  'depth_block'
    c: PointOnObject(g13,g-2)
    c: Distance(g13,g12) = 2.9  'depth_block_base'
    c: Distance(g-1,g10) = 22  'height_duct_top'
    c: Distance(g-1,g11) = 2.5  'block_rise'
FEATURE [PartDesign::Pad] Pad028  label="hfd_duct_top"
  BaseFeature = -> Pad025
  Direction = (0,0,1)
  Length = 2.8
  Length2 = 10
  Profile = -> Sketch094
  ReferenceAxis = -> Sketch094 [N_Axis]
  Refine = true
  SideType = 0
  Suppressed = false
  Type = 0
  Type2 = 0
  expr: Length = <<hfd_duct_top_s>>.Constraints.extrude
FEATURE [PartDesign::Chamfer] Chamfer037  label="hfd_outer_chmf"
  Angle = 45
  Base = -> Pad028 [Edge35,Edge34,Edge14,Edge36,Edge63,Edge39,Edge16,Edge43,Edge42,Edge41,Edge15,Edge17,Edge44,Edge62,Edge40,Edge170,Edge97,Edge47,Edge169,Edge163,Edge164,Edge165,Edge162,Edge166,Edge167,Edge168,Edge95,Edge45]
  BaseFeature = -> Pad028
  ChamferType = 0
  FlipDirection = false
  Refine = true
  Size = 0.4
  Size2 = 1
  SupportTransform = false
  Suppressed = false
  UseAllEdges = false
FEATURE [Sketcher::SketchObject] Sketch096  label="hfd_wire_tie_slot_s"
  ArcFitTolerance = 1e-06
  AttachmentOffset = pos=(0,0,6) rot=(0,0,1;0rad)
  AttachmentSupport = -> [XY_Plane140]
  ExternalTypes = [0]
  FullyConstrained = true
  MakeInternals = false
  MapMode = 5
  Placement = pos=(0,0,6) rot=(0,0,1;0rad)
  _ExternalGeoVersion = 0
  expr: .AttachmentOffset.Base.z = <<hfd_side_s>>.Constraints.tab_plane
  expr: .Constraints.base_length = <<hfd_base_s>>.Constraints.base_length
  expr: .Constraints.side_inner = <<hfd_base_s>>.Constraints.base_width - 2 * <<hfd_side_s>>.Constraints.side_width
  sketch-geometry (13):
    g0: Circle CenterX=24.1 CenterY=-75.3129 CenterZ=0 NormalX=0 NormalY=0 NormalZ=1 AngleXU=0 Radius=5.5
    g1: Circle CenterX=24.1 CenterY=-75.3129 CenterZ=0 NormalX=0 NormalY=0 NormalZ=1 AngleXU=0 Radius=7
    g2: Circle CenterX=-24.1 CenterY=-75.3129 CenterZ=0 NormalX=0 NormalY=0 NormalZ=1 AngleXU=0 Radius=5.5
    g3: Circle CenterX=-24.1 CenterY=-75.3129 CenterZ=0 NormalX=0 NormalY=0 NormalZ=1 AngleXU=0 Radius=7
    g4: LineSegment [constr] StartX=-24.1 StartY=-75.3129 StartZ=0 EndX=0 EndY=-75.3129 EndZ=0
    g5: LineSegment [constr] StartX=0 StartY=-75.3129 StartZ=0 EndX=24.1 EndY=-75.3129 EndZ=0
    g6: LineSegment [constr] StartX=24.1 StartY=-69.8129 StartZ=0 EndX=24.1 EndY=-68.3129 EndZ=0
    g7: LineSegment [constr] StartX=-28 StartY=-69.5 StartZ=0 EndX=-28 EndY=-81.1258 EndZ=0
    g8: LineSegment [constr] StartX=28 StartY=-69.5 StartZ=0 EndX=28 EndY=-81.1258 EndZ=0
    g9: LineSegment [constr] StartX=-28 StartY=-75.3129 StartZ=0 EndX=-29.6 EndY=-75.3129 EndZ=0
    g10: GeomPoint [constr] X=-28 Y=-71.4348 Z=0
    g11: GeomPoint [constr] X=-28 Y=-79.1911 Z=0
    g12: GeomPoint [constr] X=-28 Y=-80 Z=0
  constraints (37):
    c: Coincident(g1,g0)
    c: Coincident(g3,g2)
    c: Equal(g0,g2)
    c: Equal(g1,g3)
    c: Coincident(g4,g2)
    c: PointOnObject(g4,g-2)
    c: Coincident(g5,g4)
    c: Coincident(g5,g0)
    c: Horizontal(g5)
    c: Horizontal(g4)
    c: Equal(g5,g4)
    c: PointOnObject(g6,g0)
    c: PointOnObject(g6,g1)
    c: Vertical(g6)
    c: PointOnObject(g0,g6)
    c: Distance(g6,g6) = 1.5  'tie_thickness'
    c: Radius(g2) = 5.5  'loop_radius'
    c: DistanceY(g4,g-1) = 75.3129  'slot_front_inset'
    c: Vertical(g7)
    c: PointOnObject(g7,g3)
    c: PointOnObject(g7,g3)
    c: PointOnObject(g8,g1)
    c: Vertical(g8)
    c: Symmetric(g7,g8,g-2)
    c: DistanceX(g7,g8) = 56  'side_inner'
    c: Horizontal(g9)
    c: PointOnObject(g9,g2)
    c: PointOnObject(g9,g7)
    c: PointOnObject(g2,g9)
    c: Distance(g9,g9) = 1.6  'inset_depth'
    c: PointOnObject(g10,g2)
    c: PointOnObject(g11,g2)
    c: PointOnObject(g11,g7)
    c: PointOnObject(g10,g7)
    c: PointOnObject(g12,g7)
    c: DistanceY(g12,g-1) = 80  'base_length'
    c: DistanceY(g12,g7) = 10.5  'slot_end_inset'
FEATURE [PartDesign::Pocket] Pocket033  label="hfd_wire_tie_slot"
  BaseFeature = -> Chamfer037
  Direction = (0,0,-1)
  Length = 3
  Length2 = 5
  Profile = -> Sketch096
  ReferenceAxis = -> Sketch096 [N_Axis]
  Refine = true
  SideType = 0
  Suppressed = false
  Type = 0
  Type2 = 0
FEATURE [PartDesign::Fillet] Fillet017  label="hfd_wire_tie_slot_flt"
  Base = -> Pocket033 [Edge120,Edge124,Edge243,Edge245]
  BaseFeature = -> Pocket033
  Radius = 0.4
  Refine = true
  SupportTransform = false
  Suppressed = false
  UseAllEdges = false
FEATURE [PartDesign::Body] Body050  label="heater_fan_duct"
  AllowCompound = false
  Group = -> [Sketch,Pad,Sketch089,Pad023,Sketch090,Pad024,Chamfer,Fillet016,Sketch091,Pocket031,Sketch092,Pocket032,Sketch093,Pad025,Sketch094,Pad028,Chamfer037,Sketch096,Pocket033,Fillet017]
  Origin = -> Origin140
  Tip = -> Fillet017
COMPONENT P4 — recipe-attached ("heater_fan_screw_spacer001", modeled in this document).
Construction recipe (the document's own serialized feature program — sketch geometry with constraints, then the solid features built on it; lengths are millimeters unless a unit is written):

FEATURE [Sketcher::SketchObject] Sketch095  label="hfss_s"
  ArcFitTolerance = 1e-06
  AttachmentSupport = -> [XY_Plane141]
  ExternalTypes = [0]
  FullyConstrained = true
  MakeInternals = false
  MapMode = 5
  _ExternalGeoVersion = 0
  sketch-geometry (10):
    g0: Circle [constr] CenterX=0 CenterY=0 CenterZ=0 NormalX=0 NormalY=0 NormalZ=1 AngleXU=0 Radius=1.45
    g1: Circle [constr] CenterX=0 CenterY=0 CenterZ=0 NormalX=0 NormalY=0 NormalZ=1 AngleXU=0 Radius=2.25
    g2: Circle CenterX=0 CenterY=0 CenterZ=0 NormalX=0 NormalY=0 NormalZ=1 AngleXU=0 Radius=2.2
    g3: Circle CenterX=0 CenterY=0 CenterZ=0 NormalX=0 NormalY=0 NormalZ=1 AngleXU=0 Radius=1.55
    g4: GeomPoint X=-2.25 Y=0 Z=0
    g5: GeomPoint X=-2.2 Y=0 Z=0
    g6: GeomPoint X=1.55 Y=0 Z=0
    g7: GeomPoint X=1.45 Y=0 Z=0
    g8: GeomPoint X=0 Y=-2.2 Z=0
    g9: GeomPoint X=0 Y=-1.55 Z=0
  constraints (23):
    c: Coincident(g0,g-1)
    c: Coincident(g1,g0)
    c: Diameter(g0) = 2.9  'screw_diam'
    c: Diameter(g1) = 4.5  'fan_hole_diam'
    c: Coincident(g2,g0)
    c: Coincident(g3,g0)
    c: PointOnObject(g4,g1)
    c: PointOnObject(g5,g2)
    c: PointOnObject(g6,g3)
    c: PointOnObject(g7,g0)
    c: PointOnObject(g4,g-1)
    c: PointOnObject(g5,g-1)
    c: PointOnObject(g7,g-1)
    c: PointOnObject(g6,g-1)
    c: Distance(g5,g4) = 0.05  'fan_clearance'
    c: Distance(g7,g6) = 0.1  'screw_clearance'
    c: PointOnObject(g8,g2)
    c: PointOnObject(g9,g3)
    c: PointOnObject(g9,g-2)
    c: PointOnObject(g8,g-2)
    c: Distance(g9,g8) = 0.65  'thickness'
    c: Diameter(g3) = 3.1  'inner_diam'
    c: Diameter(g2) = 4.4  'outer_diam'
FEATURE [PartDesign::Pad] Pad027  label="hfss_e"
  Direction = (0,0,1)
  Length = 14
  Length2 = 10
  Profile = -> Sketch095
  ReferenceAxis = -> Sketch095 [N_Axis]
  Refine = true
  SideType = 0
  Suppressed = false
  Type = 0
  Type2 = 0
FEATURE [PartDesign::Body] Body051  label="heater_fan_screw_spacer"
  AllowCompound = false
  Group = -> [Sketch095,Pad027]
  Origin = -> Origin141
  Tip = -> Pad027
COMPONENT P5 — same part as P4; its construction recipe is shown at P4.
COMPONENT P6 — recipe-attached ("heater_heatsink_ptc_tswitch001", modeled in this document).
Construction recipe (the document's own serialized feature program — sketch geometry with constraints, then the solid features built on it; lengths are millimeters unless a unit is written):

FEATURE [PartDesign::FeatureBase] Clone025  label="hhp_ts_cln"
  BaseFeature = -> Body057
  Suppressed = false
FEATURE [Sketcher::SketchObject] Sketch112  label="hhp_ts_pocket_s"
  ArcFitTolerance = 1e-06
  AttachmentSupport = -> [XY_Plane148]
  ExternalTypes = [0]
  FullyConstrained = true
  MakeInternals = false
  MapMode = 5
  _ExternalGeoVersion = 0
  expr: .Constraints.placement_length = <<block_params>>.tswitch_placement_length
  expr: .Constraints.placement_width = <<block_params>>.tswitch_placement_width
  expr: .Constraints.pocket_length = <<block_params>>.tswitch_pocket_length
  expr: .Constraints.pocket_width = <<block_params>>.tswitch_pocket_width
  sketch-geometry (6):
    g0: Circle [constr] CenterX=25 CenterY=9 CenterZ=0 NormalX=0 NormalY=0 NormalZ=1 AngleXU=0 Radius=4.2
    g1: Circle [constr] CenterX=25 CenterY=9 CenterZ=0 NormalX=0 NormalY=0 NormalZ=1 AngleXU=0 Radius=11.2
    g2: LineSegment StartX=13.8 StartY=13.2 StartZ=0 EndX=13.8 EndY=4.8 EndZ=0
    g3: LineSegment StartX=13.8 StartY=4.8 StartZ=0 EndX=36.2 EndY=4.8 EndZ=0
    g4: LineSegment StartX=36.2 StartY=4.8 StartZ=0 EndX=36.2 EndY=13.2 EndZ=0
    g5: LineSegment StartX=36.2 StartY=13.2 StartZ=0 EndX=13.8 EndY=13.2 EndZ=0
  constraints (17):
    c: Coincident(g1,g0)
    c: DistanceY(g-1,g0) = 9  'placement_width'
    c: DistanceX(g-1,g0) = 25  'placement_length'
    c: Coincident(g2,g3)
    c: Coincident(g3,g4)
    c: Coincident(g4,g5)
    c: Coincident(g5,g2)
    c: Vertical(g2)
    c: Vertical(g4)
    c: Horizontal(g3)
    c: Horizontal(g5)
    c: Tangent(g1,g4)
    c: Tangent(g1,g2)
    c: Tangent(g0,g5)
    c: Tangent(g0,g3)
    c: Diameter(g1) = 22.4  'pocket_length'
    c: Diameter(g0) = 8.4  'pocket_width'
FEATURE [Sketcher::SketchObject] Sketch113  label="hhp_ts_screws_s"
  ArcFitTolerance = 1e-06
  AttachmentSupport = -> [XY_Plane148]
  ExternalTypes = [0]
  FullyConstrained = true
  MakeInternals = false
  MapMode = 5
  _ExternalGeoVersion = 0
  expr: .Constraints.diam = <<block_params>>.screw_drill_diam
  expr: .Constraints.placement_length = <<block_params>>.tswitch_placement_length
  expr: .Constraints.placement_width = <<block_params>>.tswitch_placement_width
  expr: .Constraints.spacing_length = <<block_params>>.tswitch_screw_spacing_length
  expr: .Constraints.spacing_width = <<block_params>>.tswitch_screw_spacing_width
  sketch-geometry (10):
    g0: Circle [constr] CenterX=25 CenterY=9 CenterZ=0 NormalX=0 NormalY=0 NormalZ=1 AngleXU=0 Radius=5.65
    g1: Circle [constr] CenterX=25 CenterY=9 CenterZ=0 NormalX=0 NormalY=0 NormalZ=1 AngleXU=0 Radius=5.5
    g2: LineSegment [constr] StartX=19.5 StartY=14.65 StartZ=0 EndX=19.5 EndY=3.35 EndZ=0
    g3: LineSegment [constr] StartX=19.5 StartY=3.35 StartZ=0 EndX=30.5 EndY=3.35 EndZ=0
    g4: LineSegment [constr] StartX=30.5 StartY=3.35 StartZ=0 EndX=30.5 EndY=14.65 EndZ=0
    g5: LineSegment [constr] StartX=30.5 StartY=14.65 StartZ=0 EndX=19.5 EndY=14.65 EndZ=0
    g6: Circle CenterX=30.5 CenterY=14.65 CenterZ=0 NormalX=0 NormalY=0 NormalZ=1 AngleXU=0 Radius=1.25
    g7: Circle CenterX=19.5 CenterY=14.65 CenterZ=0 NormalX=0 NormalY=0 NormalZ=1 AngleXU=0 Radius=1.25
    g8: Circle CenterX=19.5 CenterY=3.35 CenterZ=0 NormalX=0 NormalY=0 NormalZ=1 AngleXU=0 Radius=1.25
    g9: Circle CenterX=30.5 CenterY=3.35 CenterZ=0 NormalX=0 NormalY=0 NormalZ=1 AngleXU=0 Radius=1.25
  constraints (25):
    c: Coincident(g1,g0)
    c: DistanceY(g-1,g0) = 9  'placement_width'
    c: DistanceX(g-1,g0) = 25  'placement_length'
    c: Coincident(g2,g3)
    c: Coincident(g3,g4)
    c: Coincident(g4,g5)
    c: Coincident(g5,g2)
    c: Vertical(g2)
    c: Vertical(g4)
    c: Horizontal(g3)
    c: Horizontal(g5)
    c: Tangent(g0,g5)
    c: Tangent(g0,g3)
    c: Tangent(g1,g4)
    c: Tangent(g1,g2)
    c: Diameter(g1) = 11  'spacing_length'
    c: Diameter(g0) = 11.3  'spacing_width'
    c: Coincident(g6,g4)
    c: Coincident(g7,g2)
    c: Coincident(g8,g2)
    c: Coincident(g9,g3)
    c: Equal(g7,g6)
    c: Equal(g6,g9)
    c: Equal(g9,g8)
    c: Diameter(g8) = 2.5  'diam'
FEATURE [PartDesign::Pocket] Pocket045  label="hhp_ts_pocket"
  BaseFeature = -> Clone025
  Direction = (0,0,-1)
  Length = 0.8
  Length2 = 5
  Profile = -> Sketch112
  ReferenceAxis = -> Sketch112 [N_Axis]
  Refine = true
  SideType = 0
  Suppressed = false
  Type = 0
  Type2 = 0
  expr: Length = <<block_params>>.tswitch_pocket_depth
FEATURE [PartDesign::Pocket] Pocket046  label="hhp_ts_screws"
  BaseFeature = -> Pocket045
  Direction = (0,0,-1)
  Length = 4.5
  Length2 = 5
  Profile = -> Sketch113
  ReferenceAxis = -> Sketch113 [N_Axis]
  Refine = true
  SideType = 0
  Suppressed = false
  Type = 0
  Type2 = 0
  expr: Length = <<block_params>>.screw_drill_depth
FEATURE [PartDesign::Body] Body058  label="heater_heatsink_ptc_tswitch"
  AllowCompound = false
  Group = -> [Clone025,Sketch112,Sketch113,Pocket045,Pocket046]
  Origin = -> Origin148
  Tip = -> Pocket046
COMPONENT P7 — recipe-attached ("heater_strap_ptc001", modeled in this document).
Construction recipe (the document's own serialized feature program — sketch geometry with constraints, then the solid features built on it; lengths are millimeters unless a unit is written):

FEATURE [Sketcher::SketchObject] Sketch087  label="hcs_ptc_s"
  ArcFitTolerance = 1e-06
  AttachmentSupport = -> [XY_Plane]
  ExternalTypes = [0]
  FullyConstrained = true
  MakeInternals = false
  MapMode = 5
  _ExternalGeoVersion = 0
  expr: .Constraints.hole_spacing = sqrt(<<block_params>>.ptc_screw_spacing_length ^ 2 + <<block_params>>.ptc_screw_spacing_width ^ 2)
  expr: .Constraints.screw_hole = <<block_params>>.strap_hole
  expr: .Constraints.width = <<block_params>>.strap_width
  sketch-geometry (6):
    g0: Circle CenterX=17.3971 CenterY=0 CenterZ=0 NormalX=0 NormalY=0 NormalZ=1 AngleXU=0 Radius=1.65
    g1: Circle CenterX=-17.3971 CenterY=0 CenterZ=0 NormalX=0 NormalY=0 NormalZ=1 AngleXU=0 Radius=1.65
    g2: LineSegment StartX=-17.3971 StartY=3.25 StartZ=0 EndX=17.3971 EndY=3.25 EndZ=0
    g3: LineSegment StartX=-17.3971 StartY=-3.25 StartZ=0 EndX=17.3971 EndY=-3.25 EndZ=0
    g4: ArcOfCircle CenterX=17.3971 CenterY=0 CenterZ=0 NormalX=0 NormalY=0 NormalZ=1 AngleXU=0 Radius=3.25 StartAngle=4.71239 EndAngle=7.85398
    g5: ArcOfCircle CenterX=-17.3971 CenterY=0 CenterZ=0 NormalX=0 NormalY=0 NormalZ=1 AngleXU=0 Radius=3.25 StartAngle=1.5708 EndAngle=4.71239
  constraints (13):
    c: Coincident(g4,g0)
    c: Coincident(g5,g1)
    c: Diameter(g1) = 3.3  'screw_hole'
    c: Equal(g5,g4)
    c: Equal(g1,g0)
    c: Diameter(g5) = 6.5  'width'
    c: Tangent(g2,g5) = 1.5708
    c: Tangent(g3,g5) = -1.5708
    c: Tangent(g2,g4) = 1.5708
    c: Tangent(g4,g3) = -1.5708
    c: Distance(g1,g0) = 34.7943  'hole_spacing'
    c: Symmetric(g0,g1,g-2)
    c: PointOnObject(g0,g-1)
FEATURE [PartDesign::Pad] Pad033  label="hcs_ptc_e"
  Direction = (0,0,1)
  Length = 0.76
  Length2 = 10
  Profile = -> Sketch087
  ReferenceAxis = -> Sketch087 [N_Axis]
  Refine = true
  SideType = 0
  Suppressed = false
  Type = 0
  Type2 = 0
  expr: Length = <<block_params>>.strap_thickness
FEATURE [PartDesign::Body] Body  label="heater_strap_ptc"
  AllowCompound = false
  Group = -> [Sketch087,Pad033]
  Origin = -> Origin
  Tip = -> Pad033
COMPONENT P8 — recipe-attached ("heater_strap_tswitch001", modeled in this document).
Construction recipe (the document's own serialized feature program — sketch geometry with constraints, then the solid features built on it; lengths are millimeters unless a unit is written):

FEATURE [Sketcher::SketchObject] Sketch088  label="hcs_tswitch_s"
  ArcFitTolerance = 1e-06
  AttachmentSupport = -> [XY_Plane139]
  ExternalTypes = [0]
  FullyConstrained = true
  MakeInternals = false
  MapMode = 5
  _ExternalGeoVersion = 0
  expr: .Constraints.hole_spacing = sqrt(<<block_params>>.tswitch_screw_spacing_length ^ 2 + <<block_params>>.tswitch_screw_spacing_width ^ 2)
  expr: .Constraints.screw_hole = <<block_params>>.strap_hole
  expr: .Constraints.width = <<block_params>>.strap_width
  sketch-geometry (6):
    g0: LineSegment StartX=7.88495 StartY=3.25 StartZ=0 EndX=-7.88495 EndY=3.25 EndZ=0
    g1: LineSegment StartX=7.88495 StartY=-3.25 StartZ=0 EndX=-7.88495 EndY=-3.25 EndZ=0
    g2: Circle CenterX=7.88495 CenterY=0 CenterZ=0 NormalX=0 NormalY=0 NormalZ=1 AngleXU=0 Radius=1.65
    g3: Circle CenterX=-7.88495 CenterY=0 CenterZ=0 NormalX=0 NormalY=0 NormalZ=1 AngleXU=0 Radius=1.65
    g4: ArcOfCircle CenterX=-7.88495 CenterY=0 CenterZ=0 NormalX=0 NormalY=0 NormalZ=1 AngleXU=0 Radius=3.25 StartAngle=1.5708 EndAngle=4.71239
    g5: ArcOfCircle CenterX=7.88495 CenterY=0 CenterZ=0 NormalX=0 NormalY=0 NormalZ=1 AngleXU=0 Radius=3.25 StartAngle=4.71239 EndAngle=7.85398
  constraints (13):
    c: Equal(g3,g2)
    c: Equal(g4,g5)
    c: Diameter(g3) = 3.3  'screw_hole'
    c: Diameter(g4) = 6.5  'width'
    c: Tangent(g4,g0) = -1.5708
    c: Tangent(g4,g1) = 1.5708
    c: Tangent(g0,g5) = -1.5708
    c: Tangent(g1,g5) = 1.5708
    c: Distance(g3,g2) = 15.7699  'hole_spacing'
    c: Coincident(g3,g4)
    c: Coincident(g2,g5)
    c: Symmetric(g3,g2,g-2)
    c: PointOnObject(g2,g-1)
FEATURE [PartDesign::Pad] Pad034  label="hcs_tswitch_e"
  Direction = (0,0,1)
  Length = 0.76
  Length2 = 10
  Profile = -> Sketch088
  ReferenceAxis = -> Sketch088 [N_Axis]
  Refine = true
  SideType = 0
  Suppressed = false
  Type = 0
  Type2 = 0
  expr: Length = <<block_params>>.strap_thickness
FEATURE [PartDesign::Body] Body049  label="heater_strap_tswitch"
  AllowCompound = false
  Group = -> [Sketch088,Pad034]
  Origin = -> Origin139
  Tip = -> Pad034
COMPONENT P9 — geometry summary ("heatset_m3_short_cnck001"; no construction recipe available for this part):
  bounding box: 4.6 x 4.6 x 3.0 mm
  tessellated surface: 11,710 triangles
  volume: 20 mm^3 (32% of its bounding box)
COMPONENT P10 — geometry summary ("heatset_m3_short_cnck002"; no construction recipe available for this part):
  bounding box: 4.6 x 4.6 x 3.0 mm
  tessellated surface: 11,710 triangles
  volume: 20 mm^3 (32% of its bounding box)
COMPONENT P11 — geometry summary ("m3x18_bhcs001"; no construction recipe available for this part):
  bounding box: 19.6 x 5.7 x 5.7 mm
  tessellated surface: 3,506 triangles
  volume: 153 mm^3 (24% of its bounding box)
  symmetry: revolution-symmetric about the z axis through its bounding-box center; mirror-symmetric across its x mid-plane, y mid-plane
COMPONENT P12 — geometry summary ("m3x18_bhcs002"; no construction recipe available for this part):
  bounding box: 19.6 x 5.7 x 5.7 mm
  tessellated surface: 3,506 triangles
  volume: 153 mm^3 (24% of its bounding box)
  symmetry: revolution-symmetric about the z axis through its bounding-box center; mirror-symmetric across its x mid-plane, y mid-plane
COMPONENT P13 — geometry summary ("m3x4_bhcs001"; no construction recipe available for this part):
  bounding box: 5.7 x 5.7 x 5.6 mm
  tessellated surface: 3,506 triangles
  volume: 54 mm^3 (30% of its bounding box)
  symmetry: revolution-symmetric about the z axis through its bounding-box center
COMPONENT P14 — geometry summary ("m3x4_bhcs002"; no construction recipe available for this part):
  bounding box: 5.7 x 5.7 x 5.6 mm
  tessellated surface: 3,506 triangles
  volume: 54 mm^3 (30% of its bounding box)
  symmetry: revolution-symmetric about the z axis through its bounding-box center
COMPONENT P15 — geometry summary ("m3x6_bhcs001"; no construction recipe available for this part):
  bounding box: 7.6 x 5.7 x 5.7 mm
  tessellated surface: 3,506 triangles
  volume: 68 mm^3 (28% of its bounding box)
  symmetry: revolution-symmetric about the x axis through its bounding-box center; mirror-symmetric across its y mid-plane
COMPONENT P16 — geometry summary ("m3x6_bhcs002"; no construction recipe available for this part):
  bounding box: 7.6 x 5.7 x 5.7 mm
  tessellated surface: 3,506 triangles
  volume: 68 mm^3 (28% of its bounding box)
  symmetry: revolution-symmetric about the x axis through its bounding-box center; mirror-symmetric across its y mid-plane
COMPONENT P17 — geometry summary ("m3x8_bhcs001"; no construction recipe available for this part):
  bounding box: 9.7 x 5.7 x 5.7 mm
  tessellated surface: 3,506 triangles
  volume: 83 mm^3 (26% of its bounding box)
  symmetry: revolution-symmetric about the z axis through its bounding-box center
COMPONENT P18 — geometry summary ("m3x8_bhcs002"; no construction recipe available for this part):
  bounding box: 9.7 x 5.7 x 5.7 mm
  tessellated surface: 3,506 triangles
  volume: 83 mm^3 (26% of its bounding box)
  symmetry: revolution-symmetric about the z axis through its bounding-box center
COMPONENT P19 — geometry summary ("m3x8_bhcs003"; no construction recipe available for this part):
  bounding box: 9.7 x 5.7 x 5.7 mm
  tessellated surface: 3,506 triangles
  volume: 83 mm^3 (26% of its bounding box)
  symmetry: revolution-symmetric about the z axis through its bounding-box center
COMPONENT P20 — geometry summary ("m3x8_bhcs004"; no construction recipe available for this part):
  bounding box: 9.7 x 5.7 x 5.7 mm
  tessellated surface: 3,506 triangles
  volume: 83 mm^3 (26% of its bounding box)
  symmetry: revolution-symmetric about the z axis through its bounding-box center
COMPONENT P21 — geometry summary ("m3x8_bhcs005"; no construction recipe available for this part):
  bounding box: 9.7 x 5.7 x 5.7 mm
  tessellated surface: 3,506 triangles
  volume: 83 mm^3 (26% of its bounding box)
  symmetry: revolution-symmetric about the z axis through its bounding-box center
COMPONENT P22 — geometry summary ("ptc_mini_element_v002"; no construction recipe available for this part):
  bounding box: 49.0 x 20.8 x 5.3 mm
  tessellated surface: 13,092 triangles
  volume: 3562 mm^3 (66% of its bounding box)
  symmetry: 2-fold rotationally symmetric about the x axis; mirror-symmetric across its y mid-plane, z mid-plane
COMPONENT P23 — geometry summary ("thermal_switch_ksd9700_v002"; no construction recipe available for this part):
  bounding box: 28.0 x 8.0 x 4.0 mm
  tessellated surface: 2,600 triangles
  volume: 703 mm^3 (78% of its bounding box)
  symmetry: mirror-symmetric across its y mid-plane
COMPONENT P24 — geometry summary ("tnut_2020_m3_roll001"; no construction recipe available for this part):
  bounding box: 17.0 x 8.3 x 4.7 mm
  tessellated surface: 6,066 triangles
  volume: 406 mm^3 (61% of its bounding box)
  symmetry: mirror-symmetric across its z mid-plane
COMPONENT P25 — geometry summary ("tnut_2020_m3_roll002"; no construction recipe available for this part):
  bounding box: 17.0 x 8.3 x 4.7 mm
  tessellated surface: 6,066 triangles
  volume: 406 mm^3 (61% of its bounding box)
  symmetry: mirror-symmetric across its z mid-plane
COMPONENT P26 — geometry summary ("tnut_2020_m3_roll003"; no construction recipe available for this part):
  bounding box: 17.0 x 8.3 x 4.7 mm
  tessellated surface: 6,066 triangles
  volume: 406 mm^3 (61% of its bounding box)
  symmetry: mirror-symmetric across its z mid-plane
PROVENANCE & LICENSES
A FreeCAD (.FCStd) document from a public repository crawl; recipes are the document's own serialized feature recipes (and, for linked parts, companion documents' recipes).
License: gpl-3.0.
